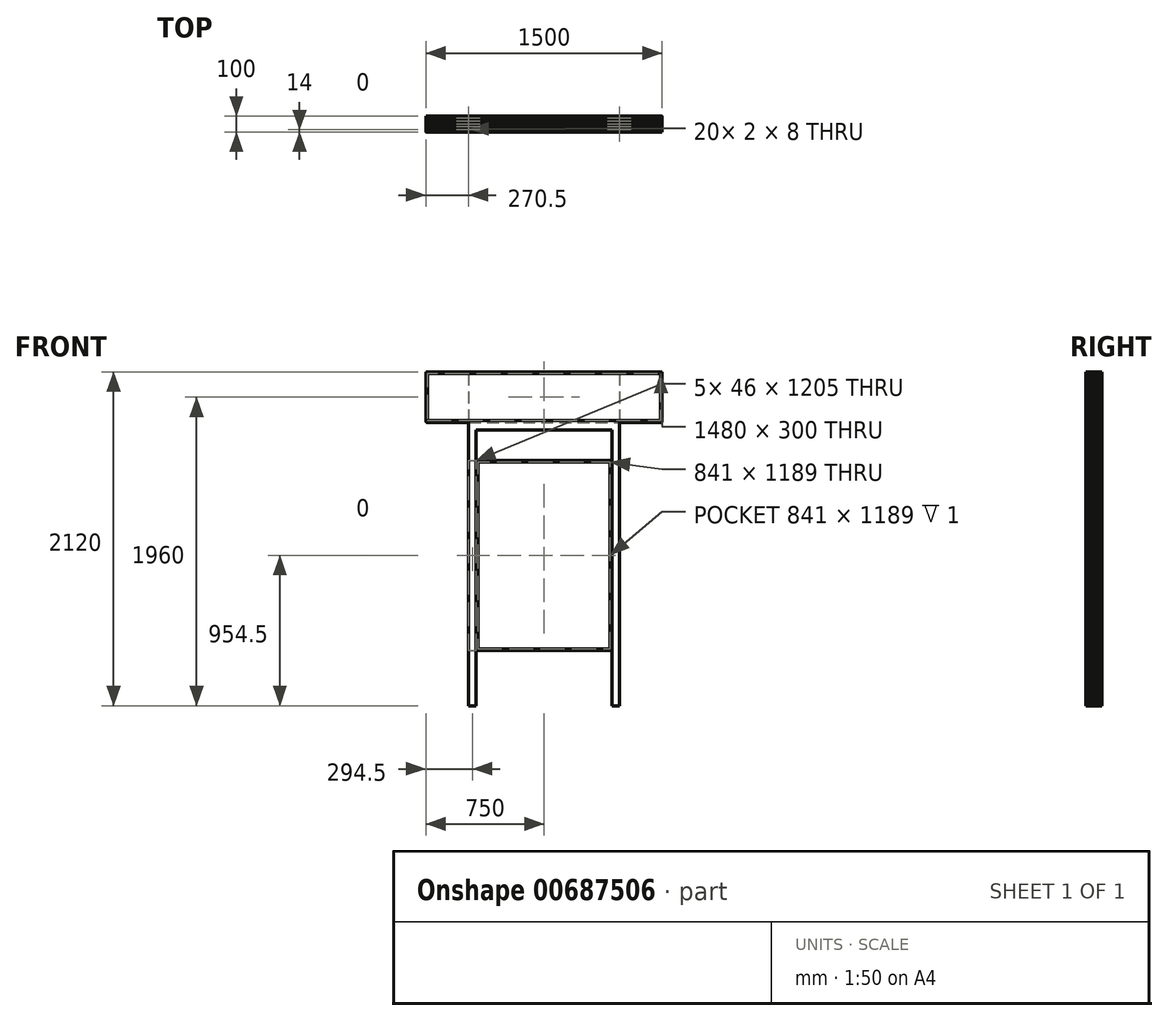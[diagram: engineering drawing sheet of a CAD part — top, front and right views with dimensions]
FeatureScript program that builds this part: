
annotation { "Feature Type Name" : "Feature", "Feature Type Description" : "" }
export const myFeature = defineFeature(function(context is Context, id is Id, definition is map)
    precondition{}
    {
        {
            var Q0;
            Q0=qCreatedBy(makeId("Front.planeOp"),FACE);
            var sketch = newSketch(context, id + "F0", { "sketchPlane" : qUnion([Q0])});
            skLineSegment(sketch, "E0.bottom", {"start": v(-480.5, 0) * mm, "end": v(-430.5, 0) * mm});
            skLineSegment(sketch, "E0.top", {"start": v(-480.5, -1800) * mm, "end": v(-430.5, -1800) * mm});
            skLineSegment(sketch, "E0.left", {"start": v(-480.5, 0) * mm, "end": v(-480.5, -1800) * mm});
            skLineSegment(sketch, "E0.right", {"start": v(-430.5, 0) * mm, "end": v(-430.5, -1800) * mm});
            skLineSegment(sketch, "E1.MirrorCS", {"start": v(480.5, -1800) * mm, "end": v(430.5, -1800) * mm});
            skLineSegment(sketch, "E2.MirrorCS", {"start": v(430.5, 0) * mm, "end": v(430.5, -1800) * mm});
            skLineSegment(sketch, "E3.MirrorCS", {"start": v(480.5, 0) * mm, "end": v(430.5, 0) * mm});
            skLineSegment(sketch, "E4.MirrorCS", {"start": v(480.5, 0) * mm, "end": v(480.5, -1800) * mm});
            skSolve(sketch);
        }
        {
            var Q0;
            Q0=qSketchRegion(id+"F0",true);
            extrude(context, id + "F1", {"entities" : qUnion([Q0]), "depth" : 100 * mm, "offsetDistance" : 25 * mm});
        }
        {
            var Q0;
            Q0=makeQuery(id+"F1.opExtrude","SWEPT_FACE",FACE,{"disambiguationData":[OSD([sQuery(id+"F0.wireOp",EDGE,"E0.bottom")])]});
            var sketch = newSketch(context, id + "F2", { "sketchPlane" : qUnion([Q0])});
            skLineSegment(sketch, "E5.bottom", {"start": v(-750, 0) * mm, "end": v(750, 0) * mm});
            skLineSegment(sketch, "E5.top", {"start": v(-750, -100) * mm, "end": v(750, -100) * mm});
            skLineSegment(sketch, "E5.left", {"start": v(-750, 0) * mm, "end": v(-750, -100) * mm});
            skLineSegment(sketch, "E5.right", {"start": v(750, 0) * mm, "end": v(750, -100) * mm});
            skSolve(sketch);
        }
        {
            var Q0;
            Q0=qSketchRegion(id+"F2",true);
            extrude(context, id + "F3", {"entities" : qUnion([Q0]), "depth" : 320 * mm, "offsetDistance" : 25 * mm});
        }
        {
            var Q0;
            Q0=makeQuery(id+"F3.opExtrude","SWEPT_FACE",FACE,{"disambiguationData":[OSD([sQuery(id+"F2.wireOp",EDGE,"E5.top")])]});
            var sketch = newSketch(context, id + "F4", { "sketchPlane" : qUnion([Q0])});
            skLineSegment(sketch, "E6.0", {"start": v(740, 310) * mm, "end": v(-740, 310) * mm});
            skLineSegment(sketch, "E6.1", {"start": v(740, 10) * mm, "end": v(740, 310) * mm});
            skLineSegment(sketch, "E6.2", {"start": v(-740, 10) * mm, "end": v(740, 10) * mm});
            skLineSegment(sketch, "E6.3", {"start": v(-740, 310) * mm, "end": v(-740, 10) * mm});
            skSolve(sketch);
        }
        {
            var Q0;
            Q0=qSketchRegion(id+"F4",true);
            extrude(context, id + "F5", {"entities" : qUnion([Q0]), "operationType" : NewBodyOperationType.REMOVE, "endBound" : BoundingType.THROUGH_ALL, "oppositeDirection" : true, "depth" : 25 * mm, "offsetDistance" : 25 * mm});
        }
        {
            var Q0;
            Q0=makeQuery(id+"F3.opExtrude","SWEPT_FACE",FACE,{"disambiguationData":[OSD([sQuery(id+"F2.wireOp",EDGE,"E5.right")])]});
            var sketch = newSketch(context, id + "F6", { "sketchPlane" : qUnion([Q0])});
            skLineSegment(sketch, "E7", {"start": v(-90, 320) * mm, "end": v(-90, 318) * mm});
            skLineSegment(sketch, "E8", {"start": v(-90, 318) * mm, "end": v(-82, 318) * mm});
            skLineSegment(sketch, "E9", {"start": v(-82, 318) * mm, "end": v(-82, 320) * mm});
            skLineSegment(sketch, "E10.1.0.0", {"start": v(-64, 318) * mm, "end": v(-64, 320) * mm});
            skLineSegment(sketch, "E10.1.0.1", {"start": v(-72, 318) * mm, "end": v(-64, 318) * mm});
            skLineSegment(sketch, "E10.1.0.2", {"start": v(-72, 320) * mm, "end": v(-72, 318) * mm});
            skLineSegment(sketch, "E10.2.0.0", {"start": v(-46, 318) * mm, "end": v(-46, 320) * mm});
            skLineSegment(sketch, "E10.2.0.1", {"start": v(-54, 318) * mm, "end": v(-46, 318) * mm});
            skLineSegment(sketch, "E10.2.0.2", {"start": v(-54, 320) * mm, "end": v(-54, 318) * mm});
            skLineSegment(sketch, "E10.3.0.0", {"start": v(-28, 318) * mm, "end": v(-28, 320) * mm});
            skLineSegment(sketch, "E10.3.0.1", {"start": v(-36, 318) * mm, "end": v(-28, 318) * mm});
            skLineSegment(sketch, "E10.3.0.2", {"start": v(-36, 320) * mm, "end": v(-36, 318) * mm});
            skLineSegment(sketch, "E10.4.0.0", {"start": v(-10, 318) * mm, "end": v(-10, 320) * mm});
            skLineSegment(sketch, "E10.4.0.1", {"start": v(-18, 318) * mm, "end": v(-10, 318) * mm});
            skLineSegment(sketch, "E10.4.0.2", {"start": v(-18, 320) * mm, "end": v(-18, 318) * mm});
            skLineSegment(sketch, "E10.direction1", {"start": v(-90, 318) * mm, "end": v(-72, 318) * mm, "construction": true});
            skLineSegment(sketch, "E11", {"start": v(-90, 320) * mm, "end": v(-82, 320) * mm});
            skLineSegment(sketch, "E12", {"start": v(-72, 320) * mm, "end": v(-64, 320) * mm});
            skLineSegment(sketch, "E13", {"start": v(-54, 320) * mm, "end": v(-46, 320) * mm});
            skLineSegment(sketch, "E14", {"start": v(-36, 320) * mm, "end": v(-28, 320) * mm});
            skLineSegment(sketch, "E15", {"start": v(-18, 320) * mm, "end": v(-10, 320) * mm});
            skLineSegment(sketch, "E16", {"start": v(0, 160) * mm, "end": v(-100, 160) * mm, "construction": true});
            skLineSegment(sketch, "E17.MirrorCS", {"start": v(-10, 2) * mm, "end": v(-10, 0) * mm});
            skLineSegment(sketch, "E18.MirrorCS", {"start": v(-36, 0) * mm, "end": v(-36, 2) * mm});
            skLineSegment(sketch, "E19.MirrorCS", {"start": v(-90, 0) * mm, "end": v(-90, 2) * mm});
            skLineSegment(sketch, "E20.MirrorCS", {"start": v(-82, 2) * mm, "end": v(-82, 0) * mm});
            skLineSegment(sketch, "E21.MirrorCS", {"start": v(-64, 2) * mm, "end": v(-64, 0) * mm});
            skLineSegment(sketch, "E22.MirrorCS", {"start": v(-72, 0) * mm, "end": v(-72, 2) * mm});
            skLineSegment(sketch, "E23.MirrorCS", {"start": v(-46, 2) * mm, "end": v(-46, 0) * mm});
            skLineSegment(sketch, "E24.MirrorCS", {"start": v(-54, 0) * mm, "end": v(-54, 2) * mm});
            skLineSegment(sketch, "E25.MirrorCS", {"start": v(-28, 2) * mm, "end": v(-28, 0) * mm});
            skLineSegment(sketch, "E26.MirrorCS", {"start": v(-18, 0) * mm, "end": v(-18, 2) * mm});
            skLineSegment(sketch, "E27.MirrorCS", {"start": v(-90, 0) * mm, "end": v(-82, 0) * mm});
            skLineSegment(sketch, "E28.MirrorCS", {"start": v(-90, 2) * mm, "end": v(-82, 2) * mm});
            skLineSegment(sketch, "E29.MirrorCS", {"start": v(-36, 2) * mm, "end": v(-28, 2) * mm});
            skLineSegment(sketch, "E30.MirrorCS", {"start": v(-36, 0) * mm, "end": v(-28, 0) * mm});
            skLineSegment(sketch, "E31.MirrorCS", {"start": v(-18, 0) * mm, "end": v(-10, 0) * mm});
            skLineSegment(sketch, "E32.MirrorCS", {"start": v(-72, 0) * mm, "end": v(-64, 0) * mm});
            skLineSegment(sketch, "E33.MirrorCS", {"start": v(-18, 2) * mm, "end": v(-10, 2) * mm});
            skLineSegment(sketch, "E34.MirrorCS", {"start": v(-90, 2) * mm, "end": v(-72, 2) * mm, "construction": true});
            skLineSegment(sketch, "E35.MirrorCS", {"start": v(-54, 0) * mm, "end": v(-46, 0) * mm});
            skLineSegment(sketch, "E36.MirrorCS", {"start": v(-72, 2) * mm, "end": v(-64, 2) * mm});
            skLineSegment(sketch, "E37.MirrorCS", {"start": v(-54, 2) * mm, "end": v(-46, 2) * mm});
            skSolve(sketch);
        }
        {
            var Q0;
            Q0=qSketchRegion(id+"F6",true);
            extrude(context, id + "F7", {"entities" : qUnion([Q0]), "operationType" : NewBodyOperationType.REMOVE, "endBound" : BoundingType.THROUGH_ALL, "oppositeDirection" : true, "depth" : 25 * mm, "offsetDistance" : 25 * mm});
        }
        {
            var Q0;
            Q0=makeQuery(id+"F3.opExtrude","SWEPT_FACE",FACE,{"disambiguationData":[OSD([sQuery(id+"F2.wireOp",EDGE,"E5.top")])]});
            cPlane(context, id + "F8", {"entities" : qUnion([Q0]), "cplaneType" : CPlaneType.OFFSET, "offset" : 1 * mm, "oppositeDirection" : true, "width" : 150 * mm, "height" : 150 * mm});
        }
        {
            var Q0;
            Q0=qCreatedBy(id+"F8.planeOp",FACE);
            var sketch = newSketch(context, id + "F9", { "sketchPlane" : qUnion([Q0])});
            skLineSegment(sketch, "E38.0", {"start": v(-740, 10) * mm, "end": v(740, 10) * mm});
            skLineSegment(sketch, "E38.1", {"start": v(-740, 310) * mm, "end": v(-740, 10) * mm});
            skLineSegment(sketch, "E38.2", {"start": v(740, 310) * mm, "end": v(-740, 310) * mm});
            skLineSegment(sketch, "E38.3", {"start": v(740, 10) * mm, "end": v(740, 310) * mm});
            skSolve(sketch);
        }
        {
            var Q0;
            Q0=qSketchRegion(id+"F9",true);
            var Q1;
            Q1=makeQuery(id+"F3.opExtrude","SWEPT_FACE",FACE,{"disambiguationData":[OSD([sQuery(id+"F2.wireOp",EDGE,"E5.bottom")])]});
            extrude(context, id + "F10", {"entities" : qUnion([Q0]), "endBound" : BoundingType.UP_TO_SURFACE, "oppositeDirection" : true, "depth" : 25 * mm, "endBoundEntityFace" : qUnion([Q1]), "hasOffset" : true, "offsetDistance" : 1 * mm});
        }
        {
            var Q0;
            {var subQ0=sQuery(id+"F2.wireOp",EDGE,"E5.top");var subQ1=sQuery(id+"F2.wireOp",EDGE,"E5.left");var subQ2=sQuery(id+"F2.wireOp",EDGE,"E5.right");Q0=makeQuery(id+"F7.boolean.opBoolean","SPLIT",FACE,{"disambiguationData":[TD([makeQuery(id+"F3.opExtrude","SWEPT_FACE",FACE,{"disambiguationData":[OSD([subQ0])]})])],"derivedFrom":makeQuery(id+"F3.opExtrude","CAP_FACE",FACE,{"disambiguationData":[OSD([sQuery(id+"F2.wireOp",EDGE,"E5.bottom"),subQ0,subQ1,subQ2])],"isStart":false})});}
            var sketch = newSketch(context, id + "F11", { "sketchPlane" : qUnion([Q0])});
            skLineSegment(sketch, "E39.0", {"start": v(-750, -18) * mm, "end": v(-750, -10) * mm});
            skLineSegment(sketch, "E39.1", {"start": v(-750, -36) * mm, "end": v(-750, -28) * mm});
            skLineSegment(sketch, "E39.2", {"start": v(-750, -54) * mm, "end": v(-750, -46) * mm});
            skLineSegment(sketch, "E39.3", {"start": v(-750, -72) * mm, "end": v(-750, -64) * mm});
            skLineSegment(sketch, "E39.4", {"start": v(-750, -90) * mm, "end": v(-750, -82) * mm});
            skLineSegment(sketch, "E40", {"start": v(-750, -10) * mm, "end": v(-748, -10) * mm});
            skLineSegment(sketch, "E41", {"start": v(-748, -10) * mm, "end": v(-748, -18) * mm});
            skLineSegment(sketch, "E42", {"start": v(-748, -90) * mm, "end": v(-750, -90) * mm});
            skLineSegment(sketch, "E43.0", {"start": v(-750, -18) * mm, "end": v(-748, -18) * mm});
            skLineSegment(sketch, "E43.1", {"start": v(-750, -28) * mm, "end": v(-748, -28) * mm});
            skLineSegment(sketch, "E43.2", {"start": v(-750, -36) * mm, "end": v(-748, -36) * mm});
            skLineSegment(sketch, "E43.3", {"start": v(-750, -46) * mm, "end": v(-748, -46) * mm});
            skLineSegment(sketch, "E43.4", {"start": v(-750, -54) * mm, "end": v(-748, -54) * mm});
            skLineSegment(sketch, "E43.5", {"start": v(-750, -64) * mm, "end": v(-748, -64) * mm});
            skLineSegment(sketch, "E43.6", {"start": v(-750, -72) * mm, "end": v(-748, -72) * mm});
            skLineSegment(sketch, "E43.7", {"start": v(-750, -82) * mm, "end": v(-748, -82) * mm});
            skLineSegment(sketch, "E44.trimOffspring", {"start": v(-748, -82) * mm, "end": v(-748, -90) * mm});
            skPoint(sketch, "E45.orphan", {"position": v(750, -82) * mm});
            skPoint(sketch, "E46.orphan", {"position": v(750, -72) * mm});
            skPoint(sketch, "E47.orphan", {"position": v(750, -64) * mm});
            skLineSegment(sketch, "E48.trimOffspring", {"start": v(-748, -64) * mm, "end": v(-748, -72) * mm});
            skPoint(sketch, "E49.orphan", {"position": v(750, -54) * mm});
            skPoint(sketch, "E50.orphan", {"position": v(750, -46) * mm});
            skLineSegment(sketch, "E51.trimOffspring", {"start": v(-748, -46) * mm, "end": v(-748, -54) * mm});
            skPoint(sketch, "E52.orphan", {"position": v(750, -36) * mm});
            skPoint(sketch, "E53.orphan", {"position": v(750, -28) * mm});
            skLineSegment(sketch, "E54.trimOffspring", {"start": v(-748, -28) * mm, "end": v(-748, -36) * mm});
            skPoint(sketch, "E55.orphan", {"position": v(750, -18) * mm});
            skLineSegment(sketch, "E56.MirrorCS", {"start": v(748, -46) * mm, "end": v(748, -54) * mm});
            skLineSegment(sketch, "E57.MirrorCS", {"start": v(748, -28) * mm, "end": v(748, -36) * mm});
            skLineSegment(sketch, "E58.MirrorCS", {"start": v(750, -64) * mm, "end": v(748, -64) * mm});
            skLineSegment(sketch, "E59.MirrorCS", {"start": v(750, -46) * mm, "end": v(748, -46) * mm});
            skLineSegment(sketch, "E60.MirrorCS", {"start": v(750, -54) * mm, "end": v(748, -54) * mm});
            skLineSegment(sketch, "E61.MirrorCS", {"start": v(750, -28) * mm, "end": v(748, -28) * mm});
            skLineSegment(sketch, "E62.MirrorCS", {"start": v(750, -36) * mm, "end": v(748, -36) * mm});
            skLineSegment(sketch, "E63.MirrorCS", {"start": v(750, -54) * mm, "end": v(750, -46) * mm});
            skLineSegment(sketch, "E64.MirrorCS", {"start": v(750, -36) * mm, "end": v(750, -28) * mm});
            skLineSegment(sketch, "E65.MirrorCS", {"start": v(750, -10) * mm, "end": v(748, -10) * mm});
            skLineSegment(sketch, "E66.MirrorCS", {"start": v(748, -64) * mm, "end": v(748, -72) * mm});
            skLineSegment(sketch, "E67.MirrorCS", {"start": v(750, -18) * mm, "end": v(748, -18) * mm});
            skLineSegment(sketch, "E68.MirrorCS", {"start": v(750, -72) * mm, "end": v(748, -72) * mm});
            skLineSegment(sketch, "E69.MirrorCS", {"start": v(748, -10) * mm, "end": v(748, -18) * mm});
            skLineSegment(sketch, "E70.MirrorCS", {"start": v(750, -72) * mm, "end": v(750, -64) * mm});
            skLineSegment(sketch, "E71.MirrorCS", {"start": v(748, -90) * mm, "end": v(750, -90) * mm});
            skLineSegment(sketch, "E72.MirrorCS", {"start": v(750, -82) * mm, "end": v(748, -82) * mm});
            skLineSegment(sketch, "E73.MirrorCS", {"start": v(750, -18) * mm, "end": v(750, -10) * mm});
            skLineSegment(sketch, "E74.MirrorCS", {"start": v(750, -90) * mm, "end": v(750, -82) * mm});
            skLineSegment(sketch, "E75.MirrorCS", {"start": v(748, -82) * mm, "end": v(748, -90) * mm});
            skSolve(sketch);
        }
        {
            var Q0;
            Q0 = qSketchRegion(id + "F11", true);
            extrude(context, id + "F12", {"entities" : qUnion([Q0]), "operationType" : NewBodyOperationType.REMOVE, "endBound" : BoundingType.THROUGH_ALL, "oppositeDirection" : true, "depth" : 25 * mm, "offsetDistance" : 25 * mm});
        }
        {
            var Q0;
            Q0=makeQuery(id+"F1.opExtrude","CAP_FACE",FACE,{"disambiguationData":[OSD([sQuery(id+"F0.wireOp",EDGE,"E1.MirrorCS"),sQuery(id+"F0.wireOp",EDGE,"E2.MirrorCS"),sQuery(id+"F0.wireOp",EDGE,"E3.MirrorCS"),sQuery(id+"F0.wireOp",EDGE,"E4.MirrorCS")])],"isStart":true});
            var sketch = newSketch(context, id + "F13", { "sketchPlane" : qUnion([Q0])});
            skLineSegment(sketch, "E76.bottom", {"start": v(-430.5, 0) * mm, "end": v(430.5, 0) * mm});
            skLineSegment(sketch, "E76.top", {"start": v(-430.5, -50) * mm, "end": v(430.5, -50) * mm});
            skLineSegment(sketch, "E76.left", {"start": v(-430.5, 0) * mm, "end": v(-430.5, -50) * mm});
            skLineSegment(sketch, "E76.right", {"start": v(430.5, 0) * mm, "end": v(430.5, -50) * mm});
            skSolve(sketch);
        }
        {
            var Q0;
            Q0 = qSketchRegion(id + "F13", true);
            var Q1;
            Q1=makeQuery(id+"F1.opExtrude","CAP_FACE",FACE,{"disambiguationData":[OSD([sQuery(id+"F0.wireOp",EDGE,"E0.bottom"),sQuery(id+"F0.wireOp",EDGE,"E0.top"),sQuery(id+"F0.wireOp",EDGE,"E0.left"),sQuery(id+"F0.wireOp",EDGE,"E0.right")])],"isStart":false});
            extrude(context, id + "F14", {"entities" : qUnion([Q0]), "operationType" : NewBodyOperationType.ADD, "endBound" : BoundingType.UP_TO_SURFACE, "oppositeDirection" : true, "depth" : 25 * mm, "endBoundEntityFace" : qUnion([Q1]), "offsetDistance" : 25 * mm});
        }
        {
            var Q0;
            Q0=makeQuery(id+"F14.boolean.opBoolean","MERGE",FACE,{"derivedFrom":[makeQuery(id+"F1.opExtrude","CAP_FACE",FACE,{"disambiguationData":[OSD([sQuery(id+"F0.wireOp",EDGE,"E0.bottom"),sQuery(id+"F0.wireOp",EDGE,"E0.top"),sQuery(id+"F0.wireOp",EDGE,"E0.left"),sQuery(id+"F0.wireOp",EDGE,"E0.right")])],"isStart":false}),makeQuery(id+"F1.opExtrude","CAP_FACE",FACE,{"disambiguationData":[OSD([sQuery(id+"F0.wireOp",EDGE,"E1.MirrorCS"),sQuery(id+"F0.wireOp",EDGE,"E2.MirrorCS"),sQuery(id+"F0.wireOp",EDGE,"E3.MirrorCS"),sQuery(id+"F0.wireOp",EDGE,"E4.MirrorCS")])],"isStart":false}),makeQuery(id+"F14.opExtrude","CAP_FACE",FACE,{"disambiguationData":[OSD([sQuery(id+"F13.wireOp",EDGE,"E76.bottom"),sQuery(id+"F13.wireOp",EDGE,"E76.top"),sQuery(id+"F13.wireOp",EDGE,"E76.left"),sQuery(id+"F13.wireOp",EDGE,"E76.right")])],"isStart":false})]});
            var sketch = newSketch(context, id + "F15", { "sketchPlane" : qUnion([Q0])});
            skLineSegment(sketch, "E77.bottom", {"start": v(-430.5, -241) * mm, "end": v(430.5, -241) * mm});
            skLineSegment(sketch, "E77.top", {"start": v(-430.5, -1450) * mm, "end": v(430.5, -1450) * mm});
            skLineSegment(sketch, "E77.left", {"start": v(-430.5, -241) * mm, "end": v(-430.5, -1450) * mm});
            skLineSegment(sketch, "E77.right", {"start": v(430.5, -241) * mm, "end": v(430.5, -1450) * mm});
            skLineSegment(sketch, "E78.0", {"start": v(-420.5, -251) * mm, "end": v(-420.5, -1440) * mm});
            skLineSegment(sketch, "E78.1", {"start": v(-420.5, -251) * mm, "end": v(420.5, -251) * mm});
            skLineSegment(sketch, "E78.2", {"start": v(420.5, -251) * mm, "end": v(420.5, -1440) * mm});
            skLineSegment(sketch, "E78.3", {"start": v(-420.5, -1440) * mm, "end": v(420.5, -1440) * mm});
            skSolve(sketch);
        }
        {
            var Q0;
            Q0 = qSketchRegion(id + "F15", true);
            extrude(context, id + "F16", {"entities" : qUnion([Q0]), "oppositeDirection" : true, "depth" : 100 * mm, "offsetDistance" : 25 * mm});
        }
        {
            var Q0;
            Q0=makeQuery(id+"F10.opExtrude","CAP_FACE",FACE,{"disambiguationData":[OSD([sQuery(id+"F9.wireOp",EDGE,"E38.0"),sQuery(id+"F9.wireOp",EDGE,"E38.1"),sQuery(id+"F9.wireOp",EDGE,"E38.2"),sQuery(id+"F9.wireOp",EDGE,"E38.3")])],"isStart":true});
            var sketch = newSketch(context, id + "F17", { "sketchPlane" : qUnion([Q0])});
            skLineSegment(sketch, "E79.0", {"start": v(-420.5, -251) * mm, "end": v(420.5, -251) * mm});
            skLineSegment(sketch, "E79.1", {"start": v(-420.5, -251) * mm, "end": v(-420.5, -1440) * mm});
            skLineSegment(sketch, "E79.2", {"start": v(-420.5, -1440) * mm, "end": v(420.5, -1440) * mm});
            skLineSegment(sketch, "E79.3", {"start": v(420.5, -251) * mm, "end": v(420.5, -1440) * mm});
            skSolve(sketch);
        }
        {
            var Q0;
            Q0 = qSketchRegion(id + "F17", true);
            var Q1;
            Q1=makeQuery(id+"F16.opExtrude","CAP_FACE",FACE,{"disambiguationData":[OSD([sQuery(id+"F15.wireOp",EDGE,"E77.bottom"),sQuery(id+"F15.wireOp",EDGE,"E77.top"),sQuery(id+"F15.wireOp",EDGE,"E77.left"),sQuery(id+"F15.wireOp",EDGE,"E77.right"),sQuery(id+"F15.wireOp",EDGE,"E78.0"),sQuery(id+"F15.wireOp",EDGE,"E78.1"),sQuery(id+"F15.wireOp",EDGE,"E78.2"),sQuery(id+"F15.wireOp",EDGE,"E78.3")])],"isStart":false});
            extrude(context, id + "F18", {"entities" : qUnion([Q0]), "operationType" : NewBodyOperationType.ADD, "endBound" : BoundingType.UP_TO_SURFACE, "oppositeDirection" : true, "depth" : 25 * mm, "endBoundEntityFace" : qUnion([Q1]), "hasOffset" : true, "offsetDistance" : 1 * mm});
        }
        {
            var Q0;
            Q0=makeQuery(id+"F16.opExtrude","SWEPT_FACE",FACE,{"disambiguationData":[OSD([sQuery(id+"F15.wireOp",EDGE,"E77.right")])]});
            var sketch = newSketch(context, id + "F19", { "sketchPlane" : qUnion([Q0])});
            skLineSegment(sketch, "E80.bottom", {"start": v(-90, -241) * mm, "end": v(-82, -241) * mm});
            skLineSegment(sketch, "E80.top", {"start": v(-90, -243) * mm, "end": v(-82, -243) * mm});
            skLineSegment(sketch, "E80.left", {"start": v(-90, -241) * mm, "end": v(-90, -243) * mm});
            skLineSegment(sketch, "E80.right", {"start": v(-82, -241) * mm, "end": v(-82, -243) * mm});
            skLineSegment(sketch, "E81.1.0.0", {"start": v(-72, -241) * mm, "end": v(-72, -243) * mm});
            skLineSegment(sketch, "E81.1.0.1", {"start": v(-64, -241) * mm, "end": v(-64, -243) * mm});
            skLineSegment(sketch, "E81.1.0.2", {"start": v(-72, -243) * mm, "end": v(-64, -243) * mm});
            skLineSegment(sketch, "E81.1.0.3", {"start": v(-72, -241) * mm, "end": v(-64, -241) * mm});
            skLineSegment(sketch, "E81.2.0.0", {"start": v(-54, -241) * mm, "end": v(-54, -243) * mm});
            skLineSegment(sketch, "E81.2.0.1", {"start": v(-46, -241) * mm, "end": v(-46, -243) * mm});
            skLineSegment(sketch, "E81.2.0.2", {"start": v(-54, -243) * mm, "end": v(-46, -243) * mm});
            skLineSegment(sketch, "E81.2.0.3", {"start": v(-54, -241) * mm, "end": v(-46, -241) * mm});
            skLineSegment(sketch, "E81.3.0.0", {"start": v(-36, -241) * mm, "end": v(-36, -243) * mm});
            skLineSegment(sketch, "E81.3.0.1", {"start": v(-28, -241) * mm, "end": v(-28, -243) * mm});
            skLineSegment(sketch, "E81.3.0.2", {"start": v(-36, -243) * mm, "end": v(-28, -243) * mm});
            skLineSegment(sketch, "E81.3.0.3", {"start": v(-36, -241) * mm, "end": v(-28, -241) * mm});
            skLineSegment(sketch, "E81.4.0.0", {"start": v(-18, -241) * mm, "end": v(-18, -243) * mm});
            skLineSegment(sketch, "E81.4.0.1", {"start": v(-10, -241) * mm, "end": v(-10, -243) * mm});
            skLineSegment(sketch, "E81.4.0.2", {"start": v(-18, -243) * mm, "end": v(-10, -243) * mm});
            skLineSegment(sketch, "E81.4.0.3", {"start": v(-18, -241) * mm, "end": v(-10, -241) * mm});
            skLineSegment(sketch, "E81.direction1", {"start": v(-90, -243) * mm, "end": v(-72, -243) * mm, "construction": true});
            skLineSegment(sketch, "E82", {"start": v(-100, -845.5) * mm, "end": v(0, -845.5) * mm, "construction": true});
            skLineSegment(sketch, "E83.MirrorCS", {"start": v(-90, -1450) * mm, "end": v(-90, -1448) * mm});
            skLineSegment(sketch, "E84.MirrorCS", {"start": v(-64, -1450) * mm, "end": v(-64, -1448) * mm});
            skLineSegment(sketch, "E85.MirrorCS", {"start": v(-90, -1448) * mm, "end": v(-82, -1448) * mm});
            skLineSegment(sketch, "E86.MirrorCS", {"start": v(-54, -1450) * mm, "end": v(-54, -1448) * mm});
            skLineSegment(sketch, "E87.MirrorCS", {"start": v(-18, -1450) * mm, "end": v(-18, -1448) * mm});
            skLineSegment(sketch, "E88.MirrorCS", {"start": v(-72, -1450) * mm, "end": v(-72, -1448) * mm});
            skLineSegment(sketch, "E89.MirrorCS", {"start": v(-10, -1450) * mm, "end": v(-10, -1448) * mm});
            skLineSegment(sketch, "E90.MirrorCS", {"start": v(-36, -1450) * mm, "end": v(-28, -1450) * mm});
            skLineSegment(sketch, "E91.MirrorCS", {"start": v(-36, -1448) * mm, "end": v(-28, -1448) * mm});
            skLineSegment(sketch, "E92.MirrorCS", {"start": v(-72, -1448) * mm, "end": v(-64, -1448) * mm});
            skLineSegment(sketch, "E93.MirrorCS", {"start": v(-18, -1448) * mm, "end": v(-10, -1448) * mm});
            skLineSegment(sketch, "E94.MirrorCS", {"start": v(-46, -1450) * mm, "end": v(-46, -1448) * mm});
            skLineSegment(sketch, "E95.MirrorCS", {"start": v(-72, -1450) * mm, "end": v(-64, -1450) * mm});
            skLineSegment(sketch, "E96.MirrorCS", {"start": v(-90, -1448) * mm, "end": v(-72, -1448) * mm, "construction": true});
            skLineSegment(sketch, "E97.MirrorCS", {"start": v(-90, -1450) * mm, "end": v(-82, -1450) * mm});
            skLineSegment(sketch, "E98.MirrorCS", {"start": v(-54, -1448) * mm, "end": v(-46, -1448) * mm});
            skLineSegment(sketch, "E99.MirrorCS", {"start": v(-36, -1450) * mm, "end": v(-36, -1448) * mm});
            skLineSegment(sketch, "E100.MirrorCS", {"start": v(-82, -1450) * mm, "end": v(-82, -1448) * mm});
            skLineSegment(sketch, "E101.MirrorCS", {"start": v(-28, -1450) * mm, "end": v(-28, -1448) * mm});
            skLineSegment(sketch, "E102.MirrorCS", {"start": v(-54, -1450) * mm, "end": v(-46, -1450) * mm});
            skLineSegment(sketch, "E103.MirrorCS", {"start": v(-18, -1450) * mm, "end": v(-10, -1450) * mm});
            skSolve(sketch);
        }
        {
            var Q0;
            Q0 = qSketchRegion(id + "F19", true);
            extrude(context, id + "F20", {"entities" : qUnion([Q0]), "operationType" : NewBodyOperationType.REMOVE, "endBound" : BoundingType.THROUGH_ALL, "oppositeDirection" : true, "depth" : 25 * mm, "offsetDistance" : 25 * mm});
        }
        {
            var Q0;
            {var subQ0=sQuery(id+"F2.wireOp",EDGE,"E5.right");var subQ1=sQuery(id+"F2.wireOp",EDGE,"E5.top");Q0=makeQuery(id+"F7.boolean.opBoolean","SPLIT",EDGE,{"disambiguationData":[TD([makeQuery(id+"F3.opExtrude","SWEPT_FACE",FACE,{"disambiguationData":[OSD([subQ1])]})])],"derivedFrom":makeQuery(id+"F3.opExtrude","CAP_EDGE",EDGE,{"disambiguationData":[OSD([subQ0])],"isStart":true})});}
            var Q1;
            Q1=makeQuery(id+"F12.boolean.opBoolean","INTERSECT",EDGE,{"derivedFrom":[makeQuery(id+"F7.boolean.opBoolean","COPY",FACE,{"derivedFrom":makeQuery(id+"F7.opExtrude","SWEPT_FACE",FACE,{"disambiguationData":[OSD([sQuery(id+"F6.wireOp",EDGE,"E28.MirrorCS")])]})}),makeQuery(id+"F12.opExtrude","SWEPT_FACE",FACE,{"disambiguationData":[OSD([sQuery(id+"F11.wireOp",EDGE,"E75.MirrorCS")])]})]});
            var Q2;
            {var subQ0=sQuery(id+"F2.wireOp",EDGE,"E5.right");Q2=makeQuery(id+"F7.boolean.opBoolean","SPLIT",EDGE,{"disambiguationData":[TD([makeQuery(id+"F7.opExtrude","SWEPT_FACE",FACE,{"disambiguationData":[OSD([sQuery(id+"F6.wireOp",EDGE,"E20.MirrorCS")])]})])],"derivedFrom":makeQuery(id+"F3.opExtrude","CAP_EDGE",EDGE,{"disambiguationData":[OSD([subQ0])],"isStart":true})});}
            var Q3;
            Q3=makeQuery(id+"F12.boolean.opBoolean","INTERSECT",EDGE,{"derivedFrom":[makeQuery(id+"F7.boolean.opBoolean","COPY",FACE,{"derivedFrom":makeQuery(id+"F7.opExtrude","SWEPT_FACE",FACE,{"disambiguationData":[OSD([sQuery(id+"F6.wireOp",EDGE,"E36.MirrorCS")])]})}),makeQuery(id+"F12.opExtrude","SWEPT_FACE",FACE,{"disambiguationData":[OSD([sQuery(id+"F11.wireOp",EDGE,"E66.MirrorCS")])]})]});
            var Q4;
            {var subQ0=sQuery(id+"F2.wireOp",EDGE,"E5.right");Q4=makeQuery(id+"F7.boolean.opBoolean","SPLIT",EDGE,{"disambiguationData":[TD([makeQuery(id+"F7.opExtrude","SWEPT_FACE",FACE,{"disambiguationData":[OSD([sQuery(id+"F6.wireOp",EDGE,"E21.MirrorCS")])]})])],"derivedFrom":makeQuery(id+"F3.opExtrude","CAP_EDGE",EDGE,{"disambiguationData":[OSD([subQ0])],"isStart":true})});}
            var Q5;
            Q5=makeQuery(id+"F12.boolean.opBoolean","INTERSECT",EDGE,{"derivedFrom":[makeQuery(id+"F7.boolean.opBoolean","COPY",FACE,{"derivedFrom":makeQuery(id+"F7.opExtrude","SWEPT_FACE",FACE,{"disambiguationData":[OSD([sQuery(id+"F6.wireOp",EDGE,"E37.MirrorCS")])]})}),makeQuery(id+"F12.opExtrude","SWEPT_FACE",FACE,{"disambiguationData":[OSD([sQuery(id+"F11.wireOp",EDGE,"E56.MirrorCS")])]})]});
            var Q6;
            {var subQ0=sQuery(id+"F2.wireOp",EDGE,"E5.right");Q6=makeQuery(id+"F7.boolean.opBoolean","SPLIT",EDGE,{"disambiguationData":[TD([makeQuery(id+"F7.opExtrude","SWEPT_FACE",FACE,{"disambiguationData":[OSD([sQuery(id+"F6.wireOp",EDGE,"E18.MirrorCS")])]})])],"derivedFrom":makeQuery(id+"F3.opExtrude","CAP_EDGE",EDGE,{"disambiguationData":[OSD([subQ0])],"isStart":true})});}
            var Q7;
            Q7=makeQuery(id+"F12.boolean.opBoolean","INTERSECT",EDGE,{"derivedFrom":[makeQuery(id+"F7.boolean.opBoolean","COPY",FACE,{"derivedFrom":makeQuery(id+"F7.opExtrude","SWEPT_FACE",FACE,{"disambiguationData":[OSD([sQuery(id+"F6.wireOp",EDGE,"E29.MirrorCS")])]})}),makeQuery(id+"F12.opExtrude","SWEPT_FACE",FACE,{"disambiguationData":[OSD([sQuery(id+"F11.wireOp",EDGE,"E57.MirrorCS")])]})]});
            var Q8;
            {var subQ0=sQuery(id+"F2.wireOp",EDGE,"E5.right");Q8=makeQuery(id+"F7.boolean.opBoolean","SPLIT",EDGE,{"disambiguationData":[TD([makeQuery(id+"F7.opExtrude","SWEPT_FACE",FACE,{"disambiguationData":[OSD([sQuery(id+"F6.wireOp",EDGE,"E25.MirrorCS")])]})])],"derivedFrom":makeQuery(id+"F3.opExtrude","CAP_EDGE",EDGE,{"disambiguationData":[OSD([subQ0])],"isStart":true})});}
            var Q9;
            Q9=makeQuery(id+"F12.boolean.opBoolean","INTERSECT",EDGE,{"derivedFrom":[makeQuery(id+"F7.boolean.opBoolean","COPY",FACE,{"derivedFrom":makeQuery(id+"F7.opExtrude","SWEPT_FACE",FACE,{"disambiguationData":[OSD([sQuery(id+"F6.wireOp",EDGE,"E33.MirrorCS")])]})}),makeQuery(id+"F12.opExtrude","SWEPT_FACE",FACE,{"disambiguationData":[OSD([sQuery(id+"F11.wireOp",EDGE,"E69.MirrorCS")])]})]});
            var Q10;
            {var subQ0=sQuery(id+"F2.wireOp",EDGE,"E5.bottom");var subQ1=sQuery(id+"F2.wireOp",EDGE,"E5.right");Q10=makeQuery(id+"F7.boolean.opBoolean","SPLIT",EDGE,{"disambiguationData":[TD([makeQuery(id+"F3.opExtrude","SWEPT_FACE",FACE,{"disambiguationData":[OSD([subQ0])]})])],"derivedFrom":makeQuery(id+"F3.opExtrude","CAP_EDGE",EDGE,{"disambiguationData":[OSD([subQ1])],"isStart":true})});}
            var Q11;
            {var subQ0=sQuery(id+"F2.wireOp",EDGE,"E5.right");var subQ1=sQuery(id+"F2.wireOp",EDGE,"E5.top");Q11=makeQuery(id+"F7.boolean.opBoolean","SPLIT",EDGE,{"disambiguationData":[TD([makeQuery(id+"F3.opExtrude","SWEPT_FACE",FACE,{"disambiguationData":[OSD([subQ1])]})])],"derivedFrom":makeQuery(id+"F3.opExtrude","CAP_EDGE",EDGE,{"disambiguationData":[OSD([subQ0])],"isStart":false})});}
            var Q12;
            Q12=makeQuery(id+"F12.boolean.opBoolean","INTERSECT",EDGE,{"derivedFrom":[makeQuery(id+"F7.boolean.opBoolean","COPY",FACE,{"derivedFrom":makeQuery(id+"F7.opExtrude","SWEPT_FACE",FACE,{"disambiguationData":[OSD([sQuery(id+"F6.wireOp",EDGE,"E8")])]})}),makeQuery(id+"F12.opExtrude","SWEPT_FACE",FACE,{"disambiguationData":[OSD([sQuery(id+"F11.wireOp",EDGE,"E75.MirrorCS")])]})]});
            var Q13;
            {var subQ0=sQuery(id+"F2.wireOp",EDGE,"E5.right");Q13=makeQuery(id+"F7.boolean.opBoolean","SPLIT",EDGE,{"disambiguationData":[TD([makeQuery(id+"F7.opExtrude","SWEPT_FACE",FACE,{"disambiguationData":[OSD([sQuery(id+"F6.wireOp",EDGE,"E9")])]})])],"derivedFrom":makeQuery(id+"F3.opExtrude","CAP_EDGE",EDGE,{"disambiguationData":[OSD([subQ0])],"isStart":false})});}
            var Q14;
            Q14=makeQuery(id+"F12.boolean.opBoolean","INTERSECT",EDGE,{"derivedFrom":[makeQuery(id+"F7.boolean.opBoolean","COPY",FACE,{"derivedFrom":makeQuery(id+"F7.opExtrude","SWEPT_FACE",FACE,{"disambiguationData":[OSD([sQuery(id+"F6.wireOp",EDGE,"E10.1.0.1")])]})}),makeQuery(id+"F12.opExtrude","SWEPT_FACE",FACE,{"disambiguationData":[OSD([sQuery(id+"F11.wireOp",EDGE,"E66.MirrorCS")])]})]});
            var Q15;
            {var subQ0=sQuery(id+"F2.wireOp",EDGE,"E5.right");Q15=makeQuery(id+"F7.boolean.opBoolean","SPLIT",EDGE,{"disambiguationData":[TD([makeQuery(id+"F7.opExtrude","SWEPT_FACE",FACE,{"disambiguationData":[OSD([sQuery(id+"F6.wireOp",EDGE,"E10.1.0.0")])]})])],"derivedFrom":makeQuery(id+"F3.opExtrude","CAP_EDGE",EDGE,{"disambiguationData":[OSD([subQ0])],"isStart":false})});}
            var Q16;
            Q16=makeQuery(id+"F12.boolean.opBoolean","INTERSECT",EDGE,{"derivedFrom":[makeQuery(id+"F7.boolean.opBoolean","COPY",FACE,{"derivedFrom":makeQuery(id+"F7.opExtrude","SWEPT_FACE",FACE,{"disambiguationData":[OSD([sQuery(id+"F6.wireOp",EDGE,"E10.2.0.1")])]})}),makeQuery(id+"F12.opExtrude","SWEPT_FACE",FACE,{"disambiguationData":[OSD([sQuery(id+"F11.wireOp",EDGE,"E56.MirrorCS")])]})]});
            var Q17;
            {var subQ0=sQuery(id+"F2.wireOp",EDGE,"E5.right");Q17=makeQuery(id+"F7.boolean.opBoolean","SPLIT",EDGE,{"disambiguationData":[TD([makeQuery(id+"F7.opExtrude","SWEPT_FACE",FACE,{"disambiguationData":[OSD([sQuery(id+"F6.wireOp",EDGE,"E10.2.0.0")])]})])],"derivedFrom":makeQuery(id+"F3.opExtrude","CAP_EDGE",EDGE,{"disambiguationData":[OSD([subQ0])],"isStart":false})});}
            var Q18;
            Q18=makeQuery(id+"F12.boolean.opBoolean","INTERSECT",EDGE,{"derivedFrom":[makeQuery(id+"F7.boolean.opBoolean","COPY",FACE,{"derivedFrom":makeQuery(id+"F7.opExtrude","SWEPT_FACE",FACE,{"disambiguationData":[OSD([sQuery(id+"F6.wireOp",EDGE,"E10.3.0.1")])]})}),makeQuery(id+"F12.opExtrude","SWEPT_FACE",FACE,{"disambiguationData":[OSD([sQuery(id+"F11.wireOp",EDGE,"E57.MirrorCS")])]})]});
            var Q19;
            {var subQ0=sQuery(id+"F2.wireOp",EDGE,"E5.right");Q19=makeQuery(id+"F7.boolean.opBoolean","SPLIT",EDGE,{"disambiguationData":[TD([makeQuery(id+"F7.opExtrude","SWEPT_FACE",FACE,{"disambiguationData":[OSD([sQuery(id+"F6.wireOp",EDGE,"E10.3.0.0")])]})])],"derivedFrom":makeQuery(id+"F3.opExtrude","CAP_EDGE",EDGE,{"disambiguationData":[OSD([subQ0])],"isStart":false})});}
            var Q20;
            Q20=makeQuery(id+"F12.boolean.opBoolean","INTERSECT",EDGE,{"derivedFrom":[makeQuery(id+"F7.boolean.opBoolean","COPY",FACE,{"derivedFrom":makeQuery(id+"F7.opExtrude","SWEPT_FACE",FACE,{"disambiguationData":[OSD([sQuery(id+"F6.wireOp",EDGE,"E10.4.0.1")])]})}),makeQuery(id+"F12.opExtrude","SWEPT_FACE",FACE,{"disambiguationData":[OSD([sQuery(id+"F11.wireOp",EDGE,"E69.MirrorCS")])]})]});
            var Q21;
            {var subQ0=sQuery(id+"F2.wireOp",EDGE,"E5.bottom");var subQ1=sQuery(id+"F2.wireOp",EDGE,"E5.right");Q21=makeQuery(id+"F7.boolean.opBoolean","SPLIT",EDGE,{"disambiguationData":[TD([makeQuery(id+"F3.opExtrude","SWEPT_FACE",FACE,{"disambiguationData":[OSD([subQ0])]})])],"derivedFrom":makeQuery(id+"F3.opExtrude","CAP_EDGE",EDGE,{"disambiguationData":[OSD([subQ1])],"isStart":false})});}
            var Q22;
            {var subQ0=sQuery(id+"F2.wireOp",EDGE,"E5.bottom");var subQ1=sQuery(id+"F2.wireOp",EDGE,"E5.left");Q22=makeQuery(id+"F7.boolean.opBoolean","SPLIT",EDGE,{"disambiguationData":[TD([makeQuery(id+"F3.opExtrude","SWEPT_FACE",FACE,{"disambiguationData":[OSD([subQ0])]})])],"derivedFrom":makeQuery(id+"F3.opExtrude","CAP_EDGE",EDGE,{"disambiguationData":[OSD([subQ1])],"isStart":false})});}
            var Q23;
            Q23=makeQuery(id+"F12.boolean.opBoolean","INTERSECT",EDGE,{"derivedFrom":[makeQuery(id+"F7.boolean.opBoolean","COPY",FACE,{"derivedFrom":makeQuery(id+"F7.opExtrude","SWEPT_FACE",FACE,{"disambiguationData":[OSD([sQuery(id+"F6.wireOp",EDGE,"E10.4.0.1")])]})}),makeQuery(id+"F12.opExtrude","SWEPT_FACE",FACE,{"disambiguationData":[OSD([sQuery(id+"F11.wireOp",EDGE,"E41")])]})]});
            var Q24;
            {var subQ0=sQuery(id+"F2.wireOp",EDGE,"E5.left");Q24=makeQuery(id+"F7.boolean.opBoolean","SPLIT",EDGE,{"disambiguationData":[TD([makeQuery(id+"F7.opExtrude","SWEPT_FACE",FACE,{"disambiguationData":[OSD([sQuery(id+"F6.wireOp",EDGE,"E10.3.0.0")])]})])],"derivedFrom":makeQuery(id+"F3.opExtrude","CAP_EDGE",EDGE,{"disambiguationData":[OSD([subQ0])],"isStart":false})});}
            var Q25;
            Q25=makeQuery(id+"F12.boolean.opBoolean","INTERSECT",EDGE,{"derivedFrom":[makeQuery(id+"F7.boolean.opBoolean","COPY",FACE,{"derivedFrom":makeQuery(id+"F7.opExtrude","SWEPT_FACE",FACE,{"disambiguationData":[OSD([sQuery(id+"F6.wireOp",EDGE,"E10.3.0.1")])]})}),makeQuery(id+"F12.opExtrude","SWEPT_FACE",FACE,{"disambiguationData":[OSD([sQuery(id+"F11.wireOp",EDGE,"E54.trimOffspring")])]})]});
            var Q26;
            {var subQ0=sQuery(id+"F2.wireOp",EDGE,"E5.left");Q26=makeQuery(id+"F7.boolean.opBoolean","SPLIT",EDGE,{"disambiguationData":[TD([makeQuery(id+"F7.opExtrude","SWEPT_FACE",FACE,{"disambiguationData":[OSD([sQuery(id+"F6.wireOp",EDGE,"E10.2.0.0")])]})])],"derivedFrom":makeQuery(id+"F3.opExtrude","CAP_EDGE",EDGE,{"disambiguationData":[OSD([subQ0])],"isStart":false})});}
            var Q27;
            Q27=makeQuery(id+"F12.boolean.opBoolean","INTERSECT",EDGE,{"derivedFrom":[makeQuery(id+"F7.boolean.opBoolean","COPY",FACE,{"derivedFrom":makeQuery(id+"F7.opExtrude","SWEPT_FACE",FACE,{"disambiguationData":[OSD([sQuery(id+"F6.wireOp",EDGE,"E10.2.0.1")])]})}),makeQuery(id+"F12.opExtrude","SWEPT_FACE",FACE,{"disambiguationData":[OSD([sQuery(id+"F11.wireOp",EDGE,"E51.trimOffspring")])]})]});
            var Q28;
            {var subQ0=sQuery(id+"F2.wireOp",EDGE,"E5.left");Q28=makeQuery(id+"F7.boolean.opBoolean","SPLIT",EDGE,{"disambiguationData":[TD([makeQuery(id+"F7.opExtrude","SWEPT_FACE",FACE,{"disambiguationData":[OSD([sQuery(id+"F6.wireOp",EDGE,"E10.1.0.0")])]})])],"derivedFrom":makeQuery(id+"F3.opExtrude","CAP_EDGE",EDGE,{"disambiguationData":[OSD([subQ0])],"isStart":false})});}
            var Q29;
            Q29=makeQuery(id+"F12.boolean.opBoolean","INTERSECT",EDGE,{"derivedFrom":[makeQuery(id+"F7.boolean.opBoolean","COPY",FACE,{"derivedFrom":makeQuery(id+"F7.opExtrude","SWEPT_FACE",FACE,{"disambiguationData":[OSD([sQuery(id+"F6.wireOp",EDGE,"E10.1.0.1")])]})}),makeQuery(id+"F12.opExtrude","SWEPT_FACE",FACE,{"disambiguationData":[OSD([sQuery(id+"F11.wireOp",EDGE,"E48.trimOffspring")])]})]});
            var Q30;
            {var subQ0=sQuery(id+"F2.wireOp",EDGE,"E5.left");Q30=makeQuery(id+"F7.boolean.opBoolean","SPLIT",EDGE,{"disambiguationData":[TD([makeQuery(id+"F7.opExtrude","SWEPT_FACE",FACE,{"disambiguationData":[OSD([sQuery(id+"F6.wireOp",EDGE,"E9")])]})])],"derivedFrom":makeQuery(id+"F3.opExtrude","CAP_EDGE",EDGE,{"disambiguationData":[OSD([subQ0])],"isStart":false})});}
            var Q31;
            Q31=makeQuery(id+"F12.boolean.opBoolean","INTERSECT",EDGE,{"derivedFrom":[makeQuery(id+"F7.boolean.opBoolean","COPY",FACE,{"derivedFrom":makeQuery(id+"F7.opExtrude","SWEPT_FACE",FACE,{"disambiguationData":[OSD([sQuery(id+"F6.wireOp",EDGE,"E8")])]})}),makeQuery(id+"F12.opExtrude","SWEPT_FACE",FACE,{"disambiguationData":[OSD([sQuery(id+"F11.wireOp",EDGE,"E44.trimOffspring")])]})]});
            var Q32;
            {var subQ0=sQuery(id+"F2.wireOp",EDGE,"E5.left");var subQ1=sQuery(id+"F2.wireOp",EDGE,"E5.top");Q32=makeQuery(id+"F7.boolean.opBoolean","SPLIT",EDGE,{"disambiguationData":[TD([makeQuery(id+"F3.opExtrude","SWEPT_FACE",FACE,{"disambiguationData":[OSD([subQ1])]})])],"derivedFrom":makeQuery(id+"F3.opExtrude","CAP_EDGE",EDGE,{"disambiguationData":[OSD([subQ0])],"isStart":false})});}
            var Q33;
            {var subQ0=sQuery(id+"F2.wireOp",EDGE,"E5.left");var subQ1=sQuery(id+"F2.wireOp",EDGE,"E5.top");Q33=makeQuery(id+"F7.boolean.opBoolean","SPLIT",EDGE,{"disambiguationData":[TD([makeQuery(id+"F3.opExtrude","SWEPT_FACE",FACE,{"disambiguationData":[OSD([subQ1])]})])],"derivedFrom":makeQuery(id+"F3.opExtrude","CAP_EDGE",EDGE,{"disambiguationData":[OSD([subQ0])],"isStart":true})});}
            var Q34;
            Q34=makeQuery(id+"F12.boolean.opBoolean","INTERSECT",EDGE,{"derivedFrom":[makeQuery(id+"F7.boolean.opBoolean","COPY",FACE,{"derivedFrom":makeQuery(id+"F7.opExtrude","SWEPT_FACE",FACE,{"disambiguationData":[OSD([sQuery(id+"F6.wireOp",EDGE,"E28.MirrorCS")])]})}),makeQuery(id+"F12.opExtrude","SWEPT_FACE",FACE,{"disambiguationData":[OSD([sQuery(id+"F11.wireOp",EDGE,"E44.trimOffspring")])]})]});
            var Q35;
            {var subQ0=sQuery(id+"F2.wireOp",EDGE,"E5.left");Q35=makeQuery(id+"F7.boolean.opBoolean","SPLIT",EDGE,{"disambiguationData":[TD([makeQuery(id+"F7.opExtrude","SWEPT_FACE",FACE,{"disambiguationData":[OSD([sQuery(id+"F6.wireOp",EDGE,"E20.MirrorCS")])]})])],"derivedFrom":makeQuery(id+"F3.opExtrude","CAP_EDGE",EDGE,{"disambiguationData":[OSD([subQ0])],"isStart":true})});}
            var Q36;
            Q36=makeQuery(id+"F12.boolean.opBoolean","INTERSECT",EDGE,{"derivedFrom":[makeQuery(id+"F7.boolean.opBoolean","COPY",FACE,{"derivedFrom":makeQuery(id+"F7.opExtrude","SWEPT_FACE",FACE,{"disambiguationData":[OSD([sQuery(id+"F6.wireOp",EDGE,"E36.MirrorCS")])]})}),makeQuery(id+"F12.opExtrude","SWEPT_FACE",FACE,{"disambiguationData":[OSD([sQuery(id+"F11.wireOp",EDGE,"E48.trimOffspring")])]})]});
            var Q37;
            {var subQ0=sQuery(id+"F2.wireOp",EDGE,"E5.left");Q37=makeQuery(id+"F7.boolean.opBoolean","SPLIT",EDGE,{"disambiguationData":[TD([makeQuery(id+"F7.opExtrude","SWEPT_FACE",FACE,{"disambiguationData":[OSD([sQuery(id+"F6.wireOp",EDGE,"E21.MirrorCS")])]})])],"derivedFrom":makeQuery(id+"F3.opExtrude","CAP_EDGE",EDGE,{"disambiguationData":[OSD([subQ0])],"isStart":true})});}
            var Q38;
            Q38=makeQuery(id+"F12.boolean.opBoolean","INTERSECT",EDGE,{"derivedFrom":[makeQuery(id+"F7.boolean.opBoolean","COPY",FACE,{"derivedFrom":makeQuery(id+"F7.opExtrude","SWEPT_FACE",FACE,{"disambiguationData":[OSD([sQuery(id+"F6.wireOp",EDGE,"E37.MirrorCS")])]})}),makeQuery(id+"F12.opExtrude","SWEPT_FACE",FACE,{"disambiguationData":[OSD([sQuery(id+"F11.wireOp",EDGE,"E51.trimOffspring")])]})]});
            var Q39;
            {var subQ0=sQuery(id+"F2.wireOp",EDGE,"E5.left");Q39=makeQuery(id+"F7.boolean.opBoolean","SPLIT",EDGE,{"disambiguationData":[TD([makeQuery(id+"F7.opExtrude","SWEPT_FACE",FACE,{"disambiguationData":[OSD([sQuery(id+"F6.wireOp",EDGE,"E18.MirrorCS")])]})])],"derivedFrom":makeQuery(id+"F3.opExtrude","CAP_EDGE",EDGE,{"disambiguationData":[OSD([subQ0])],"isStart":true})});}
            var Q40;
            Q40=makeQuery(id+"F12.boolean.opBoolean","INTERSECT",EDGE,{"derivedFrom":[makeQuery(id+"F7.boolean.opBoolean","COPY",FACE,{"derivedFrom":makeQuery(id+"F7.opExtrude","SWEPT_FACE",FACE,{"disambiguationData":[OSD([sQuery(id+"F6.wireOp",EDGE,"E29.MirrorCS")])]})}),makeQuery(id+"F12.opExtrude","SWEPT_FACE",FACE,{"disambiguationData":[OSD([sQuery(id+"F11.wireOp",EDGE,"E54.trimOffspring")])]})]});
            var Q41;
            {var subQ0=sQuery(id+"F2.wireOp",EDGE,"E5.left");Q41=makeQuery(id+"F7.boolean.opBoolean","SPLIT",EDGE,{"disambiguationData":[TD([makeQuery(id+"F7.opExtrude","SWEPT_FACE",FACE,{"disambiguationData":[OSD([sQuery(id+"F6.wireOp",EDGE,"E25.MirrorCS")])]})])],"derivedFrom":makeQuery(id+"F3.opExtrude","CAP_EDGE",EDGE,{"disambiguationData":[OSD([subQ0])],"isStart":true})});}
            var Q42;
            Q42=makeQuery(id+"F12.boolean.opBoolean","INTERSECT",EDGE,{"derivedFrom":[makeQuery(id+"F7.boolean.opBoolean","COPY",FACE,{"derivedFrom":makeQuery(id+"F7.opExtrude","SWEPT_FACE",FACE,{"disambiguationData":[OSD([sQuery(id+"F6.wireOp",EDGE,"E33.MirrorCS")])]})}),makeQuery(id+"F12.opExtrude","SWEPT_FACE",FACE,{"disambiguationData":[OSD([sQuery(id+"F11.wireOp",EDGE,"E41")])]})]});
            var Q43;
            {var subQ0=sQuery(id+"F2.wireOp",EDGE,"E5.bottom");var subQ1=sQuery(id+"F2.wireOp",EDGE,"E5.left");Q43=makeQuery(id+"F7.boolean.opBoolean","SPLIT",EDGE,{"disambiguationData":[TD([makeQuery(id+"F3.opExtrude","SWEPT_FACE",FACE,{"disambiguationData":[OSD([subQ0])]})])],"derivedFrom":makeQuery(id+"F3.opExtrude","CAP_EDGE",EDGE,{"disambiguationData":[OSD([subQ1])],"isStart":true})});}
            fillet(context, id + "F21", {"entities" : qUnion([Q0, Q1, Q2, Q3, Q4, Q5, Q6, Q7, Q8, Q9, Q10, Q11, Q12, Q13, Q14, Q15, Q16, Q17, Q18, Q19, Q20, Q21, Q22, Q23, Q24, Q25, Q26, Q27, Q28, Q29, Q30, Q31, Q32, Q33, Q34, Q35, Q36, Q37, Q38, Q39, Q40, Q41, Q42, Q43]), "radius" : 5 * mm, "tangentPropagation" : true, "allowEdgeOverflow" : false});
        }
        {
            var Q0;
            Q0=makeQuery(id+"F1.opExtrude","SWEPT_FACE",FACE,{"disambiguationData":[OSD([sQuery(id+"F0.wireOp",EDGE,"E0.top")])]});
            var sketch = newSketch(context, id + "F22", { "sketchPlane" : qUnion([Q0])});
            skLineSegment(sketch, "E104.0", {"start": v(-480.5, 10) * mm, "end": v(-478.5, 10) * mm});
            skLineSegment(sketch, "E104.1", {"start": v(-480.5, 18) * mm, "end": v(-478.5, 18) * mm});
            skLineSegment(sketch, "E104.2", {"start": v(-480.5, 28) * mm, "end": v(-478.5, 28) * mm});
            skLineSegment(sketch, "E104.3", {"start": v(-480.5, 36) * mm, "end": v(-478.5, 36) * mm});
            skLineSegment(sketch, "E104.4", {"start": v(-480.5, 46) * mm, "end": v(-478.5, 46) * mm});
            skLineSegment(sketch, "E104.5", {"start": v(-480.5, 54) * mm, "end": v(-478.5, 54) * mm});
            skLineSegment(sketch, "E104.6", {"start": v(-480.5, 64) * mm, "end": v(-478.5, 64) * mm});
            skLineSegment(sketch, "E104.7", {"start": v(-480.5, 72) * mm, "end": v(-478.5, 72) * mm});
            skLineSegment(sketch, "E105.0", {"start": v(-480.5, 90) * mm, "end": v(-480.5, 82) * mm});
            skLineSegment(sketch, "E106.0", {"start": v(-478.5, 90) * mm, "end": v(-478.5, 82) * mm});
            skPoint(sketch, "E107.orphan", {"position": v(-480.5, 0) * mm});
            skPoint(sketch, "E108.orphan", {"position": v(745, 10) * mm});
            skPoint(sketch, "E109.orphan", {"position": v(745, 18) * mm});
            skPoint(sketch, "E110.orphan", {"position": v(745, 28) * mm});
            skPoint(sketch, "E111.orphan", {"position": v(745, 46) * mm});
            skPoint(sketch, "E112.orphan", {"position": v(745, 36) * mm});
            skPoint(sketch, "E113.orphan", {"position": v(745, 54) * mm});
            skPoint(sketch, "E114.orphan", {"position": v(745, 64) * mm});
            skPoint(sketch, "E115.orphan", {"position": v(745, 72) * mm});
            skPoint(sketch, "E116.orphan", {"position": v(-745, 72) * mm});
            skPoint(sketch, "E117.orphan", {"position": v(-745, 64) * mm});
            skPoint(sketch, "E118.orphan", {"position": v(-745, 54) * mm});
            skPoint(sketch, "E119.orphan", {"position": v(-745, 46) * mm});
            skPoint(sketch, "E120.orphan", {"position": v(-745, 36) * mm});
            skPoint(sketch, "E121.orphan", {"position": v(-745, 28) * mm});
            skPoint(sketch, "E122.orphan", {"position": v(-745, 18) * mm});
            skPoint(sketch, "E123.orphan", {"position": v(-745, 10) * mm});
            skLineSegment(sketch, "E124.trimOffspring", {"start": v(-478.5, 18) * mm, "end": v(-478.5, 10) * mm});
            skLineSegment(sketch, "E125.trimOffspring", {"start": v(-480.5, 18) * mm, "end": v(-480.5, 10) * mm});
            skLineSegment(sketch, "E126.trimOffspring", {"start": v(-478.5, 36) * mm, "end": v(-478.5, 28) * mm});
            skLineSegment(sketch, "E127.trimOffspring", {"start": v(-480.5, 36) * mm, "end": v(-480.5, 28) * mm});
            skLineSegment(sketch, "E128", {"start": v(-480.5, 82) * mm, "end": v(-478.5, 82) * mm});
            skLineSegment(sketch, "E129", {"start": v(-478.5, 82) * mm, "end": v(-478.5, 90) * mm});
            skLineSegment(sketch, "E130", {"start": v(-478.5, 90) * mm, "end": v(-480.5, 90) * mm});
            skLineSegment(sketch, "E131.trimOffspring", {"start": v(-480.5, 54) * mm, "end": v(-480.5, 46) * mm});
            skLineSegment(sketch, "E132.trimOffspring", {"start": v(-478.5, 54) * mm, "end": v(-478.5, 46) * mm});
            skLineSegment(sketch, "E133.trimOffspring", {"start": v(-480.5, 72) * mm, "end": v(-480.5, 64) * mm});
            skLineSegment(sketch, "E134.trimOffspring", {"start": v(-478.5, 72) * mm, "end": v(-478.5, 64) * mm});
            skPoint(sketch, "E135.orphan", {"position": v(-480.5, 100) * mm});
            skLineSegment(sketch, "E136.MirrorCS", {"start": v(478.5, 82) * mm, "end": v(478.5, 90) * mm});
            skLineSegment(sketch, "E137.MirrorCS", {"start": v(480.5, 82) * mm, "end": v(478.5, 82) * mm});
            skLineSegment(sketch, "E138.MirrorCS", {"start": v(480.5, 10) * mm, "end": v(478.5, 10) * mm});
            skLineSegment(sketch, "E139.MirrorCS", {"start": v(478.5, 90) * mm, "end": v(480.5, 90) * mm});
            skLineSegment(sketch, "E140.MirrorCS", {"start": v(480.5, 18) * mm, "end": v(478.5, 18) * mm});
            skLineSegment(sketch, "E141.MirrorCS", {"start": v(478.5, 90) * mm, "end": v(478.5, 82) * mm});
            skLineSegment(sketch, "E142.MirrorCS", {"start": v(480.5, 90) * mm, "end": v(480.5, 82) * mm});
            skLineSegment(sketch, "E143.MirrorCS", {"start": v(480.5, 54) * mm, "end": v(480.5, 46) * mm});
            skLineSegment(sketch, "E144.MirrorCS", {"start": v(478.5, 72) * mm, "end": v(478.5, 64) * mm});
            skLineSegment(sketch, "E145.MirrorCS", {"start": v(480.5, 36) * mm, "end": v(480.5, 28) * mm});
            skLineSegment(sketch, "E146.MirrorCS", {"start": v(478.5, 36) * mm, "end": v(478.5, 28) * mm});
            skLineSegment(sketch, "E147.MirrorCS", {"start": v(480.5, 18) * mm, "end": v(480.5, 10) * mm});
            skLineSegment(sketch, "E148.MirrorCS", {"start": v(480.5, 72) * mm, "end": v(480.5, 64) * mm});
            skLineSegment(sketch, "E149.MirrorCS", {"start": v(478.5, 18) * mm, "end": v(478.5, 10) * mm});
            skLineSegment(sketch, "E150.MirrorCS", {"start": v(480.5, 28) * mm, "end": v(478.5, 28) * mm});
            skLineSegment(sketch, "E151.MirrorCS", {"start": v(478.5, 54) * mm, "end": v(478.5, 46) * mm});
            skLineSegment(sketch, "E152.MirrorCS", {"start": v(480.5, 72) * mm, "end": v(478.5, 72) * mm});
            skLineSegment(sketch, "E153.MirrorCS", {"start": v(480.5, 64) * mm, "end": v(478.5, 64) * mm});
            skLineSegment(sketch, "E154.MirrorCS", {"start": v(480.5, 54) * mm, "end": v(478.5, 54) * mm});
            skLineSegment(sketch, "E155.MirrorCS", {"start": v(480.5, 46) * mm, "end": v(478.5, 46) * mm});
            skLineSegment(sketch, "E156.MirrorCS", {"start": v(480.5, 36) * mm, "end": v(478.5, 36) * mm});
            skPoint(sketch, "E157.MirrorP", {"position": v(480.5, 100) * mm});
            skPoint(sketch, "E158.MirrorP", {"position": v(480.5, 0) * mm});
            skSolve(sketch);
        }
        {
            var Q0;
            Q0 = qSketchRegion(id + "F22", true);
            extrude(context, id + "F23", {"entities" : qUnion([Q0]), "operationType" : NewBodyOperationType.REMOVE, "endBound" : BoundingType.THROUGH_ALL, "oppositeDirection" : true, "depth" : 25 * mm, "offsetDistance" : 25 * mm});
        }
        {
            var Q0;
            Q0=makeQuery(id+"F1.opExtrude","SWEPT_FACE",FACE,{"disambiguationData":[OSD([sQuery(id+"F0.wireOp",EDGE,"E0.top")])]});
            var sketch = newSketch(context, id + "F24", { "sketchPlane" : qUnion([Q0])});
            skLineSegment(sketch, "E159.0", {"start": v(-432.5, 90) * mm, "end": v(-432.5, 82) * mm});
            skPoint(sketch, "E160.0", {"position": v(-430.5, 90) * mm});
            skPoint(sketch, "E160.1", {"position": v(-430.5, 82) * mm});
            skPoint(sketch, "E160.2", {"position": v(-430.5, 72) * mm});
            skPoint(sketch, "E160.3", {"position": v(-430.5, 64) * mm});
            skPoint(sketch, "E160.4", {"position": v(-430.5, 54) * mm});
            skPoint(sketch, "E160.5", {"position": v(-430.5, 46) * mm});
            skPoint(sketch, "E160.6", {"position": v(-430.5, 36) * mm});
            skPoint(sketch, "E160.7", {"position": v(-430.5, 28) * mm});
            skPoint(sketch, "E160.8", {"position": v(-430.5, 18) * mm});
            skPoint(sketch, "E160.9", {"position": v(-430.5, 10) * mm});
            skLineSegment(sketch, "E161", {"start": v(-430.5, 10) * mm, "end": v(-432.5, 10) * mm});
            skLineSegment(sketch, "E162", {"start": v(-430.5, 10) * mm, "end": v(-430.5, 18) * mm});
            skLineSegment(sketch, "E163", {"start": v(-430.5, 18) * mm, "end": v(-432.5, 18) * mm});
            skLineSegment(sketch, "E164", {"start": v(-432.5, 28) * mm, "end": v(-430.5, 28) * mm});
            skLineSegment(sketch, "E165", {"start": v(-430.5, 28) * mm, "end": v(-430.5, 36) * mm});
            skLineSegment(sketch, "E166", {"start": v(-432.5, 36) * mm, "end": v(-430.5, 36) * mm});
            skLineSegment(sketch, "E167", {"start": v(-430.5, 46) * mm, "end": v(-432.5, 46) * mm});
            skLineSegment(sketch, "E168", {"start": v(-430.5, 46) * mm, "end": v(-430.5, 54) * mm});
            skLineSegment(sketch, "E169", {"start": v(-432.5, 54) * mm, "end": v(-430.5, 54) * mm});
            skLineSegment(sketch, "E170", {"start": v(-432.5, 64) * mm, "end": v(-430.5, 64) * mm});
            skLineSegment(sketch, "E171", {"start": v(-430.5, 64) * mm, "end": v(-430.5, 72) * mm});
            skLineSegment(sketch, "E172", {"start": v(-432.5, 72) * mm, "end": v(-430.5, 72) * mm});
            skLineSegment(sketch, "E173", {"start": v(-432.5, 82) * mm, "end": v(-430.5, 82) * mm});
            skLineSegment(sketch, "E174", {"start": v(-430.5, 82) * mm, "end": v(-430.5, 90) * mm});
            skLineSegment(sketch, "E175", {"start": v(-432.5, 90) * mm, "end": v(-430.5, 90) * mm});
            skLineSegment(sketch, "E176.trimOffspring", {"start": v(-432.5, 72) * mm, "end": v(-432.5, 64) * mm});
            skLineSegment(sketch, "E177.trimOffspring", {"start": v(-432.5, 54) * mm, "end": v(-432.5, 46) * mm});
            skLineSegment(sketch, "E178.trimOffspring", {"start": v(-432.5, 36) * mm, "end": v(-432.5, 28) * mm});
            skLineSegment(sketch, "E179.trimOffspring", {"start": v(-432.5, 18) * mm, "end": v(-432.5, 10) * mm});
            skSolve(sketch);
        }
        {
            var Q0;
            Q0 = qSketchRegion(id + "F24", true);
            var Q1;
            Q1=makeQuery(id+"F1.opExtrude","CAP_EDGE",EDGE,{"disambiguationData":[OSD([sQuery(id+"F0.wireOp",EDGE,"E0.right")])],"isStart":false});
            var Q2;
            Q2=makeQuery(id+"F14.opExtrude","CAP_EDGE",EDGE,{"disambiguationData":[OSD([sQuery(id+"F13.wireOp",EDGE,"E76.top")])],"isStart":false});
            var Q3;
            Q3=makeQuery(id+"F1.opExtrude","CAP_EDGE",EDGE,{"disambiguationData":[OSD([sQuery(id+"F0.wireOp",EDGE,"E2.MirrorCS")])],"isStart":false});
            sweep(context, id + "F25", {"operationType" : NewBodyOperationType.REMOVE, "profiles" : qUnion([Q0]), "path" : qUnion([Q1, Q2, Q3])});
        }
        {
            var Q0;
            {var subQ0=sQuery(id+"F2.wireOp",EDGE,"jYso9TrC-VrG6-bpdd-wlHX-91mLgS95FXrc.right");var subQ1=sQuery(id+"F2.wireOp",EDGE,"jYso9TrC-VrG6-bpdd-wlHX-91mLgS95FXrc.top");Q0=makeQuery(id+"F7.boolean.opBoolean","SPLIT",EDGE,{"disambiguationData":[TD([makeQuery(id+"F3.opExtrude","SWEPT_FACE",FACE,{"disambiguationData":[OSD([subQ1])]})])],"derivedFrom":makeQuery(id+"F3.opExtrude","CAP_EDGE",EDGE,{"disambiguationData":[OSD([subQ0])],"isStart":true})});}
            var Q1;
            {var subQ0=sQuery(id+"F2.wireOp",EDGE,"jYso9TrC-VrG6-bpdd-wlHX-91mLgS95FXrc.right");Q1=makeQuery(id+"F7.boolean.opBoolean","SPLIT",EDGE,{"disambiguationData":[TD([makeQuery(id+"F7.opExtrude","SWEPT_FACE",FACE,{"disambiguationData":[OSD([sQuery(id+"F6.wireOp",EDGE,"E9")])]})])],"derivedFrom":makeQuery(id+"F3.opExtrude","CAP_EDGE",EDGE,{"disambiguationData":[OSD([subQ0])],"isStart":true})});}
            var Q2;
            {var subQ0=sQuery(id+"F2.wireOp",EDGE,"jYso9TrC-VrG6-bpdd-wlHX-91mLgS95FXrc.right");Q2=makeQuery(id+"F7.boolean.opBoolean","SPLIT",EDGE,{"disambiguationData":[TD([makeQuery(id+"F7.opExtrude","SWEPT_FACE",FACE,{"disambiguationData":[OSD([sQuery(id+"F6.wireOp",EDGE,"E10.1.0.0")])]})])],"derivedFrom":makeQuery(id+"F3.opExtrude","CAP_EDGE",EDGE,{"disambiguationData":[OSD([subQ0])],"isStart":true})});}
            var Q3;
            {var subQ0=sQuery(id+"F2.wireOp",EDGE,"jYso9TrC-VrG6-bpdd-wlHX-91mLgS95FXrc.right");Q3=makeQuery(id+"F7.boolean.opBoolean","SPLIT",EDGE,{"disambiguationData":[TD([makeQuery(id+"F7.opExtrude","SWEPT_FACE",FACE,{"disambiguationData":[OSD([sQuery(id+"F6.wireOp",EDGE,"E10.2.0.0")])]})])],"derivedFrom":makeQuery(id+"F3.opExtrude","CAP_EDGE",EDGE,{"disambiguationData":[OSD([subQ0])],"isStart":true})});}
            var Q4;
            {var subQ0=sQuery(id+"F2.wireOp",EDGE,"jYso9TrC-VrG6-bpdd-wlHX-91mLgS95FXrc.right");Q4=makeQuery(id+"F7.boolean.opBoolean","SPLIT",EDGE,{"disambiguationData":[TD([makeQuery(id+"F7.opExtrude","SWEPT_FACE",FACE,{"disambiguationData":[OSD([sQuery(id+"F6.wireOp",EDGE,"E10.3.0.0")])]})])],"derivedFrom":makeQuery(id+"F3.opExtrude","CAP_EDGE",EDGE,{"disambiguationData":[OSD([subQ0])],"isStart":true})});}
            var Q5;
            {var subQ0=sQuery(id+"F2.wireOp",EDGE,"jYso9TrC-VrG6-bpdd-wlHX-91mLgS95FXrc.bottom");var subQ1=sQuery(id+"F2.wireOp",EDGE,"jYso9TrC-VrG6-bpdd-wlHX-91mLgS95FXrc.right");Q5=makeQuery(id+"F7.boolean.opBoolean","SPLIT",EDGE,{"disambiguationData":[TD([makeQuery(id+"F3.opExtrude","SWEPT_FACE",FACE,{"disambiguationData":[OSD([subQ0])]})])],"derivedFrom":makeQuery(id+"F3.opExtrude","CAP_EDGE",EDGE,{"disambiguationData":[OSD([subQ1])],"isStart":true})});}
            var Q6;
            Q6=makeQuery(id+"Fou14xSP3GQJlB0_5.boolean.opBoolean","INTERSECT",EDGE,{"derivedFrom":[makeQuery(id+"F7.boolean.opBoolean","COPY",FACE,{"disambiguationData":[TD([makeQuery(id+"F3.opExtrude","SWEPT_FACE",FACE,{"disambiguationData":[OSD([sQuery(id+"F2.wireOp",EDGE,"jYso9TrC-VrG6-bpdd-wlHX-91mLgS95FXrc.left")])]})])],"derivedFrom":makeQuery(id+"F7.opExtrude","SWEPT_FACE",FACE,{"disambiguationData":[OSD([sQuery(id+"F6.wireOp",EDGE,"E10.4.0.1")])]})}),makeQuery(id+"Fou14xSP3GQJlB0_5.opExtrude","SWEPT_FACE",FACE,{"disambiguationData":[OSD([sQuery(id+"Ffmn4ZGQaAwYWcj_5.wireOp",EDGE,"a3c56a51-e62f-46ba-aa57-5dfe259011c510.MirrorCS")])]})]});
            var Q7;
            Q7=makeQuery(id+"Fou14xSP3GQJlB0_5.boolean.opBoolean","INTERSECT",EDGE,{"derivedFrom":[makeQuery(id+"F7.boolean.opBoolean","COPY",FACE,{"disambiguationData":[TD([makeQuery(id+"F3.opExtrude","SWEPT_FACE",FACE,{"disambiguationData":[OSD([sQuery(id+"F2.wireOp",EDGE,"jYso9TrC-VrG6-bpdd-wlHX-91mLgS95FXrc.left")])]})])],"derivedFrom":makeQuery(id+"F7.opExtrude","SWEPT_FACE",FACE,{"disambiguationData":[OSD([sQuery(id+"F6.wireOp",EDGE,"E10.3.0.1")])]})}),makeQuery(id+"Fou14xSP3GQJlB0_5.opExtrude","SWEPT_FACE",FACE,{"disambiguationData":[OSD([sQuery(id+"Ffmn4ZGQaAwYWcj_5.wireOp",EDGE,"a3c56a51-e62f-46ba-aa57-5dfe259011c59.MirrorCS")])]})]});
            var Q8;
            Q8=makeQuery(id+"Fou14xSP3GQJlB0_5.boolean.opBoolean","INTERSECT",EDGE,{"derivedFrom":[makeQuery(id+"F7.boolean.opBoolean","COPY",FACE,{"disambiguationData":[TD([makeQuery(id+"F3.opExtrude","SWEPT_FACE",FACE,{"disambiguationData":[OSD([sQuery(id+"F2.wireOp",EDGE,"jYso9TrC-VrG6-bpdd-wlHX-91mLgS95FXrc.left")])]})])],"derivedFrom":makeQuery(id+"F7.opExtrude","SWEPT_FACE",FACE,{"disambiguationData":[OSD([sQuery(id+"F6.wireOp",EDGE,"E10.2.0.1")])]})}),makeQuery(id+"Fou14xSP3GQJlB0_5.opExtrude","SWEPT_FACE",FACE,{"disambiguationData":[OSD([sQuery(id+"Ffmn4ZGQaAwYWcj_5.wireOp",EDGE,"a3c56a51-e62f-46ba-aa57-5dfe259011c58.MirrorCS")])]})]});
            var Q9;
            Q9=makeQuery(id+"Fou14xSP3GQJlB0_5.boolean.opBoolean","INTERSECT",EDGE,{"derivedFrom":[makeQuery(id+"F7.boolean.opBoolean","COPY",FACE,{"disambiguationData":[TD([makeQuery(id+"F3.opExtrude","SWEPT_FACE",FACE,{"disambiguationData":[OSD([sQuery(id+"F2.wireOp",EDGE,"jYso9TrC-VrG6-bpdd-wlHX-91mLgS95FXrc.left")])]})])],"derivedFrom":makeQuery(id+"F7.opExtrude","SWEPT_FACE",FACE,{"disambiguationData":[OSD([sQuery(id+"F6.wireOp",EDGE,"E10.1.0.1")])]})}),makeQuery(id+"Fou14xSP3GQJlB0_5.opExtrude","SWEPT_FACE",FACE,{"disambiguationData":[OSD([sQuery(id+"Ffmn4ZGQaAwYWcj_5.wireOp",EDGE,"a3c56a51-e62f-46ba-aa57-5dfe259011c520.MirrorCS")])]})]});
            var Q10;
            Q10=makeQuery(id+"Fou14xSP3GQJlB0_5.boolean.opBoolean","INTERSECT",EDGE,{"derivedFrom":[makeQuery(id+"F7.boolean.opBoolean","COPY",FACE,{"disambiguationData":[TD([makeQuery(id+"F3.opExtrude","SWEPT_FACE",FACE,{"disambiguationData":[OSD([sQuery(id+"F2.wireOp",EDGE,"jYso9TrC-VrG6-bpdd-wlHX-91mLgS95FXrc.left")])]})])],"derivedFrom":makeQuery(id+"F7.opExtrude","SWEPT_FACE",FACE,{"disambiguationData":[OSD([sQuery(id+"F6.wireOp",EDGE,"E8")])]})}),makeQuery(id+"Fou14xSP3GQJlB0_5.opExtrude","SWEPT_FACE",FACE,{"disambiguationData":[OSD([sQuery(id+"Ffmn4ZGQaAwYWcj_5.wireOp",EDGE,"a3c56a51-e62f-46ba-aa57-5dfe259011c518.MirrorCS")])]})]});
            var Q11;
            {var subQ0=sQuery(id+"F2.wireOp",EDGE,"jYso9TrC-VrG6-bpdd-wlHX-91mLgS95FXrc.left");var subQ1=sQuery(id+"F2.wireOp",EDGE,"jYso9TrC-VrG6-bpdd-wlHX-91mLgS95FXrc.top");Q11=makeQuery(id+"F7.boolean.opBoolean","SPLIT",EDGE,{"disambiguationData":[TD([makeQuery(id+"F3.opExtrude","SWEPT_FACE",FACE,{"disambiguationData":[OSD([subQ1])]})])],"derivedFrom":makeQuery(id+"F3.opExtrude","CAP_EDGE",EDGE,{"disambiguationData":[OSD([subQ0])],"isStart":true})});}
            var Q12;
            {var subQ0=sQuery(id+"F2.wireOp",EDGE,"jYso9TrC-VrG6-bpdd-wlHX-91mLgS95FXrc.left");Q12=makeQuery(id+"F7.boolean.opBoolean","SPLIT",EDGE,{"disambiguationData":[TD([makeQuery(id+"F7.opExtrude","SWEPT_FACE",FACE,{"disambiguationData":[OSD([sQuery(id+"F6.wireOp",EDGE,"E9")])]})])],"derivedFrom":makeQuery(id+"F3.opExtrude","CAP_EDGE",EDGE,{"disambiguationData":[OSD([subQ0])],"isStart":true})});}
            var Q13;
            {var subQ0=sQuery(id+"F2.wireOp",EDGE,"jYso9TrC-VrG6-bpdd-wlHX-91mLgS95FXrc.left");Q13=makeQuery(id+"F7.boolean.opBoolean","SPLIT",EDGE,{"disambiguationData":[TD([makeQuery(id+"F7.opExtrude","SWEPT_FACE",FACE,{"disambiguationData":[OSD([sQuery(id+"F6.wireOp",EDGE,"E10.1.0.0")])]})])],"derivedFrom":makeQuery(id+"F3.opExtrude","CAP_EDGE",EDGE,{"disambiguationData":[OSD([subQ0])],"isStart":true})});}
            var Q14;
            {var subQ0=sQuery(id+"F2.wireOp",EDGE,"jYso9TrC-VrG6-bpdd-wlHX-91mLgS95FXrc.left");Q14=makeQuery(id+"F7.boolean.opBoolean","SPLIT",EDGE,{"disambiguationData":[TD([makeQuery(id+"F7.opExtrude","SWEPT_FACE",FACE,{"disambiguationData":[OSD([sQuery(id+"F6.wireOp",EDGE,"E10.2.0.0")])]})])],"derivedFrom":makeQuery(id+"F3.opExtrude","CAP_EDGE",EDGE,{"disambiguationData":[OSD([subQ0])],"isStart":true})});}
            var Q15;
            {var subQ0=sQuery(id+"F2.wireOp",EDGE,"jYso9TrC-VrG6-bpdd-wlHX-91mLgS95FXrc.bottom");var subQ1=sQuery(id+"F2.wireOp",EDGE,"jYso9TrC-VrG6-bpdd-wlHX-91mLgS95FXrc.left");Q15=makeQuery(id+"F7.boolean.opBoolean","SPLIT",EDGE,{"disambiguationData":[TD([makeQuery(id+"F3.opExtrude","SWEPT_FACE",FACE,{"disambiguationData":[OSD([subQ0])]})])],"derivedFrom":makeQuery(id+"F3.opExtrude","CAP_EDGE",EDGE,{"disambiguationData":[OSD([subQ1])],"isStart":true})});}
            var Q16;
            Q16=makeQuery(id+"F1.opExtrude","SWEPT_EDGE",EDGE,{"disambiguationData":[OSD([sQuery(id+"F0.wireOp",EDGE,"E3.MirrorCS"),sQuery(id+"F0.wireOp",EDGE,"E4.MirrorCS")])]});
            var Q17;
            {var subQ0=sQuery(id+"F2.wireOp",EDGE,"jYso9TrC-VrG6-bpdd-wlHX-91mLgS95FXrc.left");Q17=makeQuery(id+"F7.boolean.opBoolean","SPLIT",EDGE,{"disambiguationData":[TD([makeQuery(id+"F7.opExtrude","SWEPT_FACE",FACE,{"disambiguationData":[OSD([sQuery(id+"F6.wireOp",EDGE,"E10.3.0.0")])]})])],"derivedFrom":makeQuery(id+"F3.opExtrude","CAP_EDGE",EDGE,{"disambiguationData":[OSD([subQ0])],"isStart":true})});}
            var Q18;
            Q18=makeQuery(id+"F7.boolean.opBoolean","INTERSECT",EDGE,{"derivedFrom":[makeQuery(id+"F3.opExtrude","SWEPT_FACE",FACE,{"disambiguationData":[OSD([sQuery(id+"F2.wireOp",EDGE,"jYso9TrC-VrG6-bpdd-wlHX-91mLgS95FXrc.left")])]}),makeQuery(id+"F7.opExtrude","SWEPT_FACE",FACE,{"disambiguationData":[OSD([sQuery(id+"F6.wireOp",EDGE,"E10.4.0.1")])]})]});
            var Q19;
            Q19=makeQuery(id+"F7.boolean.opBoolean","INTERSECT",EDGE,{"derivedFrom":[makeQuery(id+"F3.opExtrude","SWEPT_FACE",FACE,{"disambiguationData":[OSD([sQuery(id+"F2.wireOp",EDGE,"jYso9TrC-VrG6-bpdd-wlHX-91mLgS95FXrc.left")])]}),makeQuery(id+"F7.opExtrude","SWEPT_FACE",FACE,{"disambiguationData":[OSD([sQuery(id+"F6.wireOp",EDGE,"E10.3.0.1")])]})]});
            var Q20;
            Q20=makeQuery(id+"F7.boolean.opBoolean","INTERSECT",EDGE,{"derivedFrom":[makeQuery(id+"F3.opExtrude","SWEPT_FACE",FACE,{"disambiguationData":[OSD([sQuery(id+"F2.wireOp",EDGE,"jYso9TrC-VrG6-bpdd-wlHX-91mLgS95FXrc.left")])]}),makeQuery(id+"F7.opExtrude","SWEPT_FACE",FACE,{"disambiguationData":[OSD([sQuery(id+"F6.wireOp",EDGE,"E10.2.0.1")])]})]});
            var Q21;
            Q21=makeQuery(id+"F7.boolean.opBoolean","INTERSECT",EDGE,{"derivedFrom":[makeQuery(id+"F3.opExtrude","SWEPT_FACE",FACE,{"disambiguationData":[OSD([sQuery(id+"F2.wireOp",EDGE,"jYso9TrC-VrG6-bpdd-wlHX-91mLgS95FXrc.left")])]}),makeQuery(id+"F7.opExtrude","SWEPT_FACE",FACE,{"disambiguationData":[OSD([sQuery(id+"F6.wireOp",EDGE,"E10.1.0.1")])]})]});
            var Q22;
            Q22=makeQuery(id+"F7.boolean.opBoolean","INTERSECT",EDGE,{"derivedFrom":[makeQuery(id+"F3.opExtrude","SWEPT_FACE",FACE,{"disambiguationData":[OSD([sQuery(id+"F2.wireOp",EDGE,"jYso9TrC-VrG6-bpdd-wlHX-91mLgS95FXrc.left")])]}),makeQuery(id+"F7.opExtrude","SWEPT_FACE",FACE,{"disambiguationData":[OSD([sQuery(id+"F6.wireOp",EDGE,"E8")])]})]});
            var Q23;
            Q23=makeQuery(id+"F1.opExtrude","SWEPT_FACE",FACE,{"disambiguationData":[OSD([sQuery(id+"F0.wireOp",EDGE,"E3.MirrorCS")])]});
            var Q24;
            {var subQ0=sQuery(id+"F2.wireOp",EDGE,"kwgpZEqd-2C8t-yznH-LOjq-w4z4yBxY72GK.right");Q24=makeQuery(id+"F7.boolean.opBoolean","SPLIT",EDGE,{"disambiguationData":[TD([makeQuery(id+"F7.opExtrude","SWEPT_FACE",FACE,{"disambiguationData":[OSD([sQuery(id+"F6.wireOp",EDGE,"E10.1.0.0")])]})])],"derivedFrom":makeQuery(id+"F3.opExtrude","CAP_EDGE",EDGE,{"disambiguationData":[OSD([subQ0])],"isStart":true})});}
            var Q25;
            {var subQ0=sQuery(id+"F2.wireOp",EDGE,"kwgpZEqd-2C8t-yznH-LOjq-w4z4yBxY72GK.right");Q25=makeQuery(id+"F7.boolean.opBoolean","SPLIT",EDGE,{"disambiguationData":[TD([makeQuery(id+"F7.opExtrude","SWEPT_FACE",FACE,{"disambiguationData":[OSD([sQuery(id+"F6.wireOp",EDGE,"E9")])]})])],"derivedFrom":makeQuery(id+"F3.opExtrude","CAP_EDGE",EDGE,{"disambiguationData":[OSD([subQ0])],"isStart":true})});}
            var Q26;
            {var subQ0=sQuery(id+"F2.wireOp",EDGE,"kwgpZEqd-2C8t-yznH-LOjq-w4z4yBxY72GK.right");var subQ1=sQuery(id+"F2.wireOp",EDGE,"kwgpZEqd-2C8t-yznH-LOjq-w4z4yBxY72GK.top");Q26=makeQuery(id+"F7.boolean.opBoolean","SPLIT",EDGE,{"disambiguationData":[TD([makeQuery(id+"F3.opExtrude","SWEPT_FACE",FACE,{"disambiguationData":[OSD([subQ1])]})])],"derivedFrom":makeQuery(id+"F3.opExtrude","CAP_EDGE",EDGE,{"disambiguationData":[OSD([subQ0])],"isStart":true})});}
            var Q27;
            {var subQ0=sQuery(id+"F2.wireOp",EDGE,"kwgpZEqd-2C8t-yznH-LOjq-w4z4yBxY72GK.right");Q27=makeQuery(id+"F7.boolean.opBoolean","SPLIT",EDGE,{"disambiguationData":[TD([makeQuery(id+"F7.opExtrude","SWEPT_FACE",FACE,{"disambiguationData":[OSD([sQuery(id+"F6.wireOp",EDGE,"E10.2.0.0")])]})])],"derivedFrom":makeQuery(id+"F3.opExtrude","CAP_EDGE",EDGE,{"disambiguationData":[OSD([subQ0])],"isStart":true})});}
            var Q28;
            {var subQ0=sQuery(id+"F2.wireOp",EDGE,"kwgpZEqd-2C8t-yznH-LOjq-w4z4yBxY72GK.right");Q28=makeQuery(id+"F7.boolean.opBoolean","SPLIT",EDGE,{"disambiguationData":[TD([makeQuery(id+"F7.opExtrude","SWEPT_FACE",FACE,{"disambiguationData":[OSD([sQuery(id+"F6.wireOp",EDGE,"E10.3.0.0")])]})])],"derivedFrom":makeQuery(id+"F3.opExtrude","CAP_EDGE",EDGE,{"disambiguationData":[OSD([subQ0])],"isStart":true})});}
            var Q29;
            {var subQ0=sQuery(id+"F2.wireOp",EDGE,"kwgpZEqd-2C8t-yznH-LOjq-w4z4yBxY72GK.bottom");var subQ1=sQuery(id+"F2.wireOp",EDGE,"kwgpZEqd-2C8t-yznH-LOjq-w4z4yBxY72GK.right");Q29=makeQuery(id+"F7.boolean.opBoolean","SPLIT",EDGE,{"disambiguationData":[TD([makeQuery(id+"F3.opExtrude","SWEPT_FACE",FACE,{"disambiguationData":[OSD([subQ0])]})])],"derivedFrom":makeQuery(id+"F3.opExtrude","CAP_EDGE",EDGE,{"disambiguationData":[OSD([subQ1])],"isStart":true})});}
            var Q30;
            Q30=makeQuery(id+"F7.boolean.opBoolean","INTERSECT",EDGE,{"derivedFrom":[makeQuery(id+"F3.opExtrude","SWEPT_FACE",FACE,{"disambiguationData":[OSD([sQuery(id+"F2.wireOp",EDGE,"kwgpZEqd-2C8t-yznH-LOjq-w4z4yBxY72GK.right")])]}),makeQuery(id+"F7.opExtrude","SWEPT_FACE",FACE,{"disambiguationData":[OSD([sQuery(id+"F6.wireOp",EDGE,"E10.4.0.1")])]})]});
            var Q31;
            Q31=makeQuery(id+"F7.boolean.opBoolean","INTERSECT",EDGE,{"derivedFrom":[makeQuery(id+"F3.opExtrude","SWEPT_FACE",FACE,{"disambiguationData":[OSD([sQuery(id+"F2.wireOp",EDGE,"kwgpZEqd-2C8t-yznH-LOjq-w4z4yBxY72GK.right")])]}),makeQuery(id+"F7.opExtrude","SWEPT_FACE",FACE,{"disambiguationData":[OSD([sQuery(id+"F6.wireOp",EDGE,"E10.3.0.1")])]})]});
            var Q32;
            Q32=makeQuery(id+"F7.boolean.opBoolean","INTERSECT",EDGE,{"derivedFrom":[makeQuery(id+"F3.opExtrude","SWEPT_FACE",FACE,{"disambiguationData":[OSD([sQuery(id+"F2.wireOp",EDGE,"kwgpZEqd-2C8t-yznH-LOjq-w4z4yBxY72GK.right")])]}),makeQuery(id+"F7.opExtrude","SWEPT_FACE",FACE,{"disambiguationData":[OSD([sQuery(id+"F6.wireOp",EDGE,"E10.2.0.1")])]})]});
            var Q33;
            Q33=makeQuery(id+"F7.boolean.opBoolean","INTERSECT",EDGE,{"derivedFrom":[makeQuery(id+"F3.opExtrude","SWEPT_FACE",FACE,{"disambiguationData":[OSD([sQuery(id+"F2.wireOp",EDGE,"kwgpZEqd-2C8t-yznH-LOjq-w4z4yBxY72GK.right")])]}),makeQuery(id+"F7.opExtrude","SWEPT_FACE",FACE,{"disambiguationData":[OSD([sQuery(id+"F6.wireOp",EDGE,"E10.1.0.1")])]})]});
            var Q34;
            Q34=makeQuery(id+"F7.boolean.opBoolean","INTERSECT",EDGE,{"derivedFrom":[makeQuery(id+"F3.opExtrude","SWEPT_FACE",FACE,{"disambiguationData":[OSD([sQuery(id+"F2.wireOp",EDGE,"kwgpZEqd-2C8t-yznH-LOjq-w4z4yBxY72GK.right")])]}),makeQuery(id+"F7.opExtrude","SWEPT_FACE",FACE,{"disambiguationData":[OSD([sQuery(id+"F6.wireOp",EDGE,"E8")])]})]});
            var Q35;
            {var subQ0=sQuery(id+"F2.wireOp",EDGE,"jYso9TrC-VrG6-bpdd-wlHX-91mLgS95FXrc.right");var subQ1=sQuery(id+"F2.wireOp",EDGE,"jYso9TrC-VrG6-bpdd-wlHX-91mLgS95FXrc.top");Q35=makeQuery(id+"F7.boolean.opBoolean","SPLIT",EDGE,{"disambiguationData":[TD([makeQuery(id+"F3.opExtrude","SWEPT_FACE",FACE,{"disambiguationData":[OSD([subQ1])]})])],"derivedFrom":makeQuery(id+"F3.opExtrude","CAP_EDGE",EDGE,{"disambiguationData":[OSD([subQ0])],"isStart":false})});}
            var Q36;
            Q36=makeQuery(id+"Fou14xSP3GQJlB0_5.boolean.opBoolean","INTERSECT",EDGE,{"derivedFrom":[makeQuery(id+"F7.boolean.opBoolean","COPY",FACE,{"disambiguationData":[TD([makeQuery(id+"F3.opExtrude","SWEPT_FACE",FACE,{"disambiguationData":[OSD([sQuery(id+"F2.wireOp",EDGE,"jYso9TrC-VrG6-bpdd-wlHX-91mLgS95FXrc.left")])]})])],"derivedFrom":makeQuery(id+"F7.opExtrude","SWEPT_FACE",FACE,{"disambiguationData":[OSD([sQuery(id+"F6.wireOp",EDGE,"E28.MirrorCS")])]})}),makeQuery(id+"Fou14xSP3GQJlB0_5.opExtrude","SWEPT_FACE",FACE,{"disambiguationData":[OSD([sQuery(id+"Ffmn4ZGQaAwYWcj_5.wireOp",EDGE,"a3c56a51-e62f-46ba-aa57-5dfe259011c518.MirrorCS")])]})]});
            var Q37;
            {var subQ0=sQuery(id+"F2.wireOp",EDGE,"jYso9TrC-VrG6-bpdd-wlHX-91mLgS95FXrc.right");Q37=makeQuery(id+"F7.boolean.opBoolean","SPLIT",EDGE,{"disambiguationData":[TD([makeQuery(id+"F7.opExtrude","SWEPT_FACE",FACE,{"disambiguationData":[OSD([sQuery(id+"F6.wireOp",EDGE,"E20.MirrorCS")])]})])],"derivedFrom":makeQuery(id+"F3.opExtrude","CAP_EDGE",EDGE,{"disambiguationData":[OSD([subQ0])],"isStart":false})});}
            var Q38;
            Q38=makeQuery(id+"Fou14xSP3GQJlB0_5.boolean.opBoolean","INTERSECT",EDGE,{"derivedFrom":[makeQuery(id+"F7.boolean.opBoolean","COPY",FACE,{"disambiguationData":[TD([makeQuery(id+"F3.opExtrude","SWEPT_FACE",FACE,{"disambiguationData":[OSD([sQuery(id+"F2.wireOp",EDGE,"jYso9TrC-VrG6-bpdd-wlHX-91mLgS95FXrc.left")])]})])],"derivedFrom":makeQuery(id+"F7.opExtrude","SWEPT_FACE",FACE,{"disambiguationData":[OSD([sQuery(id+"F6.wireOp",EDGE,"E36.MirrorCS")])]})}),makeQuery(id+"Fou14xSP3GQJlB0_5.opExtrude","SWEPT_FACE",FACE,{"disambiguationData":[OSD([sQuery(id+"Ffmn4ZGQaAwYWcj_5.wireOp",EDGE,"a3c56a51-e62f-46ba-aa57-5dfe259011c520.MirrorCS")])]})]});
            var Q39;
            {var subQ0=sQuery(id+"F2.wireOp",EDGE,"jYso9TrC-VrG6-bpdd-wlHX-91mLgS95FXrc.right");Q39=makeQuery(id+"F7.boolean.opBoolean","SPLIT",EDGE,{"disambiguationData":[TD([makeQuery(id+"F7.opExtrude","SWEPT_FACE",FACE,{"disambiguationData":[OSD([sQuery(id+"F6.wireOp",EDGE,"E21.MirrorCS")])]})])],"derivedFrom":makeQuery(id+"F3.opExtrude","CAP_EDGE",EDGE,{"disambiguationData":[OSD([subQ0])],"isStart":false})});}
            var Q40;
            Q40=makeQuery(id+"Fou14xSP3GQJlB0_5.boolean.opBoolean","INTERSECT",EDGE,{"derivedFrom":[makeQuery(id+"F7.boolean.opBoolean","COPY",FACE,{"disambiguationData":[TD([makeQuery(id+"F3.opExtrude","SWEPT_FACE",FACE,{"disambiguationData":[OSD([sQuery(id+"F2.wireOp",EDGE,"jYso9TrC-VrG6-bpdd-wlHX-91mLgS95FXrc.left")])]})])],"derivedFrom":makeQuery(id+"F7.opExtrude","SWEPT_FACE",FACE,{"disambiguationData":[OSD([sQuery(id+"F6.wireOp",EDGE,"E37.MirrorCS")])]})}),makeQuery(id+"Fou14xSP3GQJlB0_5.opExtrude","SWEPT_FACE",FACE,{"disambiguationData":[OSD([sQuery(id+"Ffmn4ZGQaAwYWcj_5.wireOp",EDGE,"a3c56a51-e62f-46ba-aa57-5dfe259011c58.MirrorCS")])]})]});
            var Q41;
            {var subQ0=sQuery(id+"F2.wireOp",EDGE,"jYso9TrC-VrG6-bpdd-wlHX-91mLgS95FXrc.right");Q41=makeQuery(id+"F7.boolean.opBoolean","SPLIT",EDGE,{"disambiguationData":[TD([makeQuery(id+"F7.opExtrude","SWEPT_FACE",FACE,{"disambiguationData":[OSD([sQuery(id+"F6.wireOp",EDGE,"E18.MirrorCS")])]})])],"derivedFrom":makeQuery(id+"F3.opExtrude","CAP_EDGE",EDGE,{"disambiguationData":[OSD([subQ0])],"isStart":false})});}
            var Q42;
            Q42=makeQuery(id+"Fou14xSP3GQJlB0_5.boolean.opBoolean","INTERSECT",EDGE,{"derivedFrom":[makeQuery(id+"F7.boolean.opBoolean","COPY",FACE,{"disambiguationData":[TD([makeQuery(id+"F3.opExtrude","SWEPT_FACE",FACE,{"disambiguationData":[OSD([sQuery(id+"F2.wireOp",EDGE,"jYso9TrC-VrG6-bpdd-wlHX-91mLgS95FXrc.left")])]})])],"derivedFrom":makeQuery(id+"F7.opExtrude","SWEPT_FACE",FACE,{"disambiguationData":[OSD([sQuery(id+"F6.wireOp",EDGE,"E29.MirrorCS")])]})}),makeQuery(id+"Fou14xSP3GQJlB0_5.opExtrude","SWEPT_FACE",FACE,{"disambiguationData":[OSD([sQuery(id+"Ffmn4ZGQaAwYWcj_5.wireOp",EDGE,"a3c56a51-e62f-46ba-aa57-5dfe259011c59.MirrorCS")])]})]});
            var Q43;
            {var subQ0=sQuery(id+"F2.wireOp",EDGE,"jYso9TrC-VrG6-bpdd-wlHX-91mLgS95FXrc.right");Q43=makeQuery(id+"F7.boolean.opBoolean","SPLIT",EDGE,{"disambiguationData":[TD([makeQuery(id+"F7.opExtrude","SWEPT_FACE",FACE,{"disambiguationData":[OSD([sQuery(id+"F6.wireOp",EDGE,"E25.MirrorCS")])]})])],"derivedFrom":makeQuery(id+"F3.opExtrude","CAP_EDGE",EDGE,{"disambiguationData":[OSD([subQ0])],"isStart":false})});}
            var Q44;
            Q44=makeQuery(id+"Fou14xSP3GQJlB0_5.boolean.opBoolean","INTERSECT",EDGE,{"derivedFrom":[makeQuery(id+"F7.boolean.opBoolean","COPY",FACE,{"disambiguationData":[TD([makeQuery(id+"F3.opExtrude","SWEPT_FACE",FACE,{"disambiguationData":[OSD([sQuery(id+"F2.wireOp",EDGE,"jYso9TrC-VrG6-bpdd-wlHX-91mLgS95FXrc.left")])]})])],"derivedFrom":makeQuery(id+"F7.opExtrude","SWEPT_FACE",FACE,{"disambiguationData":[OSD([sQuery(id+"F6.wireOp",EDGE,"E33.MirrorCS")])]})}),makeQuery(id+"Fou14xSP3GQJlB0_5.opExtrude","SWEPT_FACE",FACE,{"disambiguationData":[OSD([sQuery(id+"Ffmn4ZGQaAwYWcj_5.wireOp",EDGE,"a3c56a51-e62f-46ba-aa57-5dfe259011c510.MirrorCS")])]})]});
            var Q45;
            {var subQ0=sQuery(id+"F2.wireOp",EDGE,"jYso9TrC-VrG6-bpdd-wlHX-91mLgS95FXrc.bottom");var subQ1=sQuery(id+"F2.wireOp",EDGE,"jYso9TrC-VrG6-bpdd-wlHX-91mLgS95FXrc.right");Q45=makeQuery(id+"F7.boolean.opBoolean","SPLIT",EDGE,{"disambiguationData":[TD([makeQuery(id+"F3.opExtrude","SWEPT_FACE",FACE,{"disambiguationData":[OSD([subQ0])]})])],"derivedFrom":makeQuery(id+"F3.opExtrude","CAP_EDGE",EDGE,{"disambiguationData":[OSD([subQ1])],"isStart":false})});}
            var Q46;
            {var subQ0=sQuery(id+"F2.wireOp",EDGE,"jYso9TrC-VrG6-bpdd-wlHX-91mLgS95FXrc.left");var subQ1=sQuery(id+"F2.wireOp",EDGE,"jYso9TrC-VrG6-bpdd-wlHX-91mLgS95FXrc.top");Q46=makeQuery(id+"F7.boolean.opBoolean","SPLIT",EDGE,{"disambiguationData":[TD([makeQuery(id+"F3.opExtrude","SWEPT_FACE",FACE,{"disambiguationData":[OSD([subQ1])]})])],"derivedFrom":makeQuery(id+"F3.opExtrude","CAP_EDGE",EDGE,{"disambiguationData":[OSD([subQ0])],"isStart":false})});}
            var Q47;
            Q47=makeQuery(id+"F7.boolean.opBoolean","INTERSECT",EDGE,{"derivedFrom":[makeQuery(id+"F3.opExtrude","SWEPT_FACE",FACE,{"disambiguationData":[OSD([sQuery(id+"F2.wireOp",EDGE,"jYso9TrC-VrG6-bpdd-wlHX-91mLgS95FXrc.left")])]}),makeQuery(id+"F7.opExtrude","SWEPT_FACE",FACE,{"disambiguationData":[OSD([sQuery(id+"F6.wireOp",EDGE,"E28.MirrorCS")])]})]});
            var Q48;
            {var subQ0=sQuery(id+"F2.wireOp",EDGE,"jYso9TrC-VrG6-bpdd-wlHX-91mLgS95FXrc.left");Q48=makeQuery(id+"F7.boolean.opBoolean","SPLIT",EDGE,{"disambiguationData":[TD([makeQuery(id+"F7.opExtrude","SWEPT_FACE",FACE,{"disambiguationData":[OSD([sQuery(id+"F6.wireOp",EDGE,"E20.MirrorCS")])]})])],"derivedFrom":makeQuery(id+"F3.opExtrude","CAP_EDGE",EDGE,{"disambiguationData":[OSD([subQ0])],"isStart":false})});}
            var Q49;
            Q49=makeQuery(id+"F7.boolean.opBoolean","INTERSECT",EDGE,{"derivedFrom":[makeQuery(id+"F3.opExtrude","SWEPT_FACE",FACE,{"disambiguationData":[OSD([sQuery(id+"F2.wireOp",EDGE,"jYso9TrC-VrG6-bpdd-wlHX-91mLgS95FXrc.left")])]}),makeQuery(id+"F7.opExtrude","SWEPT_FACE",FACE,{"disambiguationData":[OSD([sQuery(id+"F6.wireOp",EDGE,"E36.MirrorCS")])]})]});
            var Q50;
            {var subQ0=sQuery(id+"F2.wireOp",EDGE,"jYso9TrC-VrG6-bpdd-wlHX-91mLgS95FXrc.left");Q50=makeQuery(id+"F7.boolean.opBoolean","SPLIT",EDGE,{"disambiguationData":[TD([makeQuery(id+"F7.opExtrude","SWEPT_FACE",FACE,{"disambiguationData":[OSD([sQuery(id+"F6.wireOp",EDGE,"E21.MirrorCS")])]})])],"derivedFrom":makeQuery(id+"F3.opExtrude","CAP_EDGE",EDGE,{"disambiguationData":[OSD([subQ0])],"isStart":false})});}
            var Q51;
            Q51=makeQuery(id+"F7.boolean.opBoolean","INTERSECT",EDGE,{"derivedFrom":[makeQuery(id+"F3.opExtrude","SWEPT_FACE",FACE,{"disambiguationData":[OSD([sQuery(id+"F2.wireOp",EDGE,"jYso9TrC-VrG6-bpdd-wlHX-91mLgS95FXrc.left")])]}),makeQuery(id+"F7.opExtrude","SWEPT_FACE",FACE,{"disambiguationData":[OSD([sQuery(id+"F6.wireOp",EDGE,"E37.MirrorCS")])]})]});
            var Q52;
            {var subQ0=sQuery(id+"F2.wireOp",EDGE,"jYso9TrC-VrG6-bpdd-wlHX-91mLgS95FXrc.left");Q52=makeQuery(id+"F7.boolean.opBoolean","SPLIT",EDGE,{"disambiguationData":[TD([makeQuery(id+"F7.opExtrude","SWEPT_FACE",FACE,{"disambiguationData":[OSD([sQuery(id+"F6.wireOp",EDGE,"E18.MirrorCS")])]})])],"derivedFrom":makeQuery(id+"F3.opExtrude","CAP_EDGE",EDGE,{"disambiguationData":[OSD([subQ0])],"isStart":false})});}
            var Q53;
            Q53=makeQuery(id+"F7.boolean.opBoolean","INTERSECT",EDGE,{"derivedFrom":[makeQuery(id+"F3.opExtrude","SWEPT_FACE",FACE,{"disambiguationData":[OSD([sQuery(id+"F2.wireOp",EDGE,"jYso9TrC-VrG6-bpdd-wlHX-91mLgS95FXrc.left")])]}),makeQuery(id+"F7.opExtrude","SWEPT_FACE",FACE,{"disambiguationData":[OSD([sQuery(id+"F6.wireOp",EDGE,"E29.MirrorCS")])]})]});
            var Q54;
            {var subQ0=sQuery(id+"F2.wireOp",EDGE,"jYso9TrC-VrG6-bpdd-wlHX-91mLgS95FXrc.left");Q54=makeQuery(id+"F7.boolean.opBoolean","SPLIT",EDGE,{"disambiguationData":[TD([makeQuery(id+"F7.opExtrude","SWEPT_FACE",FACE,{"disambiguationData":[OSD([sQuery(id+"F6.wireOp",EDGE,"E25.MirrorCS")])]})])],"derivedFrom":makeQuery(id+"F3.opExtrude","CAP_EDGE",EDGE,{"disambiguationData":[OSD([subQ0])],"isStart":false})});}
            var Q55;
            Q55=makeQuery(id+"F7.boolean.opBoolean","INTERSECT",EDGE,{"derivedFrom":[makeQuery(id+"F3.opExtrude","SWEPT_FACE",FACE,{"disambiguationData":[OSD([sQuery(id+"F2.wireOp",EDGE,"jYso9TrC-VrG6-bpdd-wlHX-91mLgS95FXrc.left")])]}),makeQuery(id+"F7.opExtrude","SWEPT_FACE",FACE,{"disambiguationData":[OSD([sQuery(id+"F6.wireOp",EDGE,"E33.MirrorCS")])]})]});
            var Q56;
            {var subQ0=sQuery(id+"F2.wireOp",EDGE,"jYso9TrC-VrG6-bpdd-wlHX-91mLgS95FXrc.bottom");var subQ1=sQuery(id+"F2.wireOp",EDGE,"jYso9TrC-VrG6-bpdd-wlHX-91mLgS95FXrc.left");Q56=makeQuery(id+"F7.boolean.opBoolean","SPLIT",EDGE,{"disambiguationData":[TD([makeQuery(id+"F3.opExtrude","SWEPT_FACE",FACE,{"disambiguationData":[OSD([subQ0])]})])],"derivedFrom":makeQuery(id+"F3.opExtrude","CAP_EDGE",EDGE,{"disambiguationData":[OSD([subQ1])],"isStart":false})});}
            var Q57;
            {var subQ0=sQuery(id+"F2.wireOp",EDGE,"kwgpZEqd-2C8t-yznH-LOjq-w4z4yBxY72GK.bottom");var subQ1=sQuery(id+"F2.wireOp",EDGE,"kwgpZEqd-2C8t-yznH-LOjq-w4z4yBxY72GK.right");Q57=makeQuery(id+"F7.boolean.opBoolean","SPLIT",EDGE,{"disambiguationData":[TD([makeQuery(id+"F3.opExtrude","SWEPT_FACE",FACE,{"disambiguationData":[OSD([subQ0])]})])],"derivedFrom":makeQuery(id+"F3.opExtrude","CAP_EDGE",EDGE,{"disambiguationData":[OSD([subQ1])],"isStart":false})});}
            var Q58;
            Q58=makeQuery(id+"F7.boolean.opBoolean","INTERSECT",EDGE,{"derivedFrom":[makeQuery(id+"F3.opExtrude","SWEPT_FACE",FACE,{"disambiguationData":[OSD([sQuery(id+"F2.wireOp",EDGE,"kwgpZEqd-2C8t-yznH-LOjq-w4z4yBxY72GK.right")])]}),makeQuery(id+"F7.opExtrude","SWEPT_FACE",FACE,{"disambiguationData":[OSD([sQuery(id+"F6.wireOp",EDGE,"E33.MirrorCS")])]})]});
            var Q59;
            {var subQ0=sQuery(id+"F2.wireOp",EDGE,"kwgpZEqd-2C8t-yznH-LOjq-w4z4yBxY72GK.right");Q59=makeQuery(id+"F7.boolean.opBoolean","SPLIT",EDGE,{"disambiguationData":[TD([makeQuery(id+"F7.opExtrude","SWEPT_FACE",FACE,{"disambiguationData":[OSD([sQuery(id+"F6.wireOp",EDGE,"E25.MirrorCS")])]})])],"derivedFrom":makeQuery(id+"F3.opExtrude","CAP_EDGE",EDGE,{"disambiguationData":[OSD([subQ0])],"isStart":false})});}
            var Q60;
            Q60=makeQuery(id+"F7.boolean.opBoolean","INTERSECT",EDGE,{"derivedFrom":[makeQuery(id+"F3.opExtrude","SWEPT_FACE",FACE,{"disambiguationData":[OSD([sQuery(id+"F2.wireOp",EDGE,"kwgpZEqd-2C8t-yznH-LOjq-w4z4yBxY72GK.right")])]}),makeQuery(id+"F7.opExtrude","SWEPT_FACE",FACE,{"disambiguationData":[OSD([sQuery(id+"F6.wireOp",EDGE,"E29.MirrorCS")])]})]});
            var Q61;
            {var subQ0=sQuery(id+"F2.wireOp",EDGE,"kwgpZEqd-2C8t-yznH-LOjq-w4z4yBxY72GK.right");Q61=makeQuery(id+"F7.boolean.opBoolean","SPLIT",EDGE,{"disambiguationData":[TD([makeQuery(id+"F7.opExtrude","SWEPT_FACE",FACE,{"disambiguationData":[OSD([sQuery(id+"F6.wireOp",EDGE,"E18.MirrorCS")])]})])],"derivedFrom":makeQuery(id+"F3.opExtrude","CAP_EDGE",EDGE,{"disambiguationData":[OSD([subQ0])],"isStart":false})});}
            var Q62;
            Q62=makeQuery(id+"F7.boolean.opBoolean","INTERSECT",EDGE,{"derivedFrom":[makeQuery(id+"F3.opExtrude","SWEPT_FACE",FACE,{"disambiguationData":[OSD([sQuery(id+"F2.wireOp",EDGE,"kwgpZEqd-2C8t-yznH-LOjq-w4z4yBxY72GK.right")])]}),makeQuery(id+"F7.opExtrude","SWEPT_FACE",FACE,{"disambiguationData":[OSD([sQuery(id+"F6.wireOp",EDGE,"E37.MirrorCS")])]})]});
            var Q63;
            {var subQ0=sQuery(id+"F2.wireOp",EDGE,"kwgpZEqd-2C8t-yznH-LOjq-w4z4yBxY72GK.right");Q63=makeQuery(id+"F7.boolean.opBoolean","SPLIT",EDGE,{"disambiguationData":[TD([makeQuery(id+"F7.opExtrude","SWEPT_FACE",FACE,{"disambiguationData":[OSD([sQuery(id+"F6.wireOp",EDGE,"E21.MirrorCS")])]})])],"derivedFrom":makeQuery(id+"F3.opExtrude","CAP_EDGE",EDGE,{"disambiguationData":[OSD([subQ0])],"isStart":false})});}
            var Q64;
            Q64=makeQuery(id+"F7.boolean.opBoolean","INTERSECT",EDGE,{"derivedFrom":[makeQuery(id+"F3.opExtrude","SWEPT_FACE",FACE,{"disambiguationData":[OSD([sQuery(id+"F2.wireOp",EDGE,"kwgpZEqd-2C8t-yznH-LOjq-w4z4yBxY72GK.right")])]}),makeQuery(id+"F7.opExtrude","SWEPT_FACE",FACE,{"disambiguationData":[OSD([sQuery(id+"F6.wireOp",EDGE,"E36.MirrorCS")])]})]});
            var Q65;
            {var subQ0=sQuery(id+"F2.wireOp",EDGE,"kwgpZEqd-2C8t-yznH-LOjq-w4z4yBxY72GK.right");Q65=makeQuery(id+"F7.boolean.opBoolean","SPLIT",EDGE,{"disambiguationData":[TD([makeQuery(id+"F7.opExtrude","SWEPT_FACE",FACE,{"disambiguationData":[OSD([sQuery(id+"F6.wireOp",EDGE,"E20.MirrorCS")])]})])],"derivedFrom":makeQuery(id+"F3.opExtrude","CAP_EDGE",EDGE,{"disambiguationData":[OSD([subQ0])],"isStart":false})});}
            var Q66;
            Q66=makeQuery(id+"F7.boolean.opBoolean","INTERSECT",EDGE,{"derivedFrom":[makeQuery(id+"F3.opExtrude","SWEPT_FACE",FACE,{"disambiguationData":[OSD([sQuery(id+"F2.wireOp",EDGE,"kwgpZEqd-2C8t-yznH-LOjq-w4z4yBxY72GK.right")])]}),makeQuery(id+"F7.opExtrude","SWEPT_FACE",FACE,{"disambiguationData":[OSD([sQuery(id+"F6.wireOp",EDGE,"E28.MirrorCS")])]})]});
            var Q67;
            {var subQ0=sQuery(id+"F2.wireOp",EDGE,"kwgpZEqd-2C8t-yznH-LOjq-w4z4yBxY72GK.right");var subQ1=sQuery(id+"F2.wireOp",EDGE,"kwgpZEqd-2C8t-yznH-LOjq-w4z4yBxY72GK.top");Q67=makeQuery(id+"F7.boolean.opBoolean","SPLIT",EDGE,{"disambiguationData":[TD([makeQuery(id+"F3.opExtrude","SWEPT_FACE",FACE,{"disambiguationData":[OSD([subQ1])]})])],"derivedFrom":makeQuery(id+"F3.opExtrude","CAP_EDGE",EDGE,{"disambiguationData":[OSD([subQ0])],"isStart":false})});}
            var Q68;
            {var subQ0=sQuery(id+"F2.wireOp",EDGE,"kwgpZEqd-2C8t-yznH-LOjq-w4z4yBxY72GK.left");var subQ1=sQuery(id+"F2.wireOp",EDGE,"kwgpZEqd-2C8t-yznH-LOjq-w4z4yBxY72GK.top");Q68=makeQuery(id+"F7.boolean.opBoolean","SPLIT",EDGE,{"disambiguationData":[TD([makeQuery(id+"F3.opExtrude","SWEPT_FACE",FACE,{"disambiguationData":[OSD([subQ1])]})])],"derivedFrom":makeQuery(id+"F3.opExtrude","CAP_EDGE",EDGE,{"disambiguationData":[OSD([subQ0])],"isStart":false})});}
            var Q69;
            {var subQ0=sQuery(id+"F2.wireOp",EDGE,"kwgpZEqd-2C8t-yznH-LOjq-w4z4yBxY72GK.left");Q69=makeQuery(id+"F7.boolean.opBoolean","SPLIT",EDGE,{"disambiguationData":[TD([makeQuery(id+"F7.opExtrude","SWEPT_FACE",FACE,{"disambiguationData":[OSD([sQuery(id+"F6.wireOp",EDGE,"E20.MirrorCS")])]})])],"derivedFrom":makeQuery(id+"F3.opExtrude","CAP_EDGE",EDGE,{"disambiguationData":[OSD([subQ0])],"isStart":false})});}
            var Q70;
            Q70=makeQuery(id+"F7.boolean.opBoolean","INTERSECT",EDGE,{"derivedFrom":[makeQuery(id+"F3.opExtrude","SWEPT_FACE",FACE,{"disambiguationData":[OSD([sQuery(id+"F2.wireOp",EDGE,"kwgpZEqd-2C8t-yznH-LOjq-w4z4yBxY72GK.left")])]}),makeQuery(id+"F7.opExtrude","SWEPT_FACE",FACE,{"disambiguationData":[OSD([sQuery(id+"F6.wireOp",EDGE,"E36.MirrorCS")])]})]});
            var Q71;
            {var subQ0=sQuery(id+"F2.wireOp",EDGE,"kwgpZEqd-2C8t-yznH-LOjq-w4z4yBxY72GK.left");Q71=makeQuery(id+"F7.boolean.opBoolean","SPLIT",EDGE,{"disambiguationData":[TD([makeQuery(id+"F7.opExtrude","SWEPT_FACE",FACE,{"disambiguationData":[OSD([sQuery(id+"F6.wireOp",EDGE,"E21.MirrorCS")])]})])],"derivedFrom":makeQuery(id+"F3.opExtrude","CAP_EDGE",EDGE,{"disambiguationData":[OSD([subQ0])],"isStart":false})});}
            var Q72;
            Q72=makeQuery(id+"F7.boolean.opBoolean","INTERSECT",EDGE,{"derivedFrom":[makeQuery(id+"F3.opExtrude","SWEPT_FACE",FACE,{"disambiguationData":[OSD([sQuery(id+"F2.wireOp",EDGE,"kwgpZEqd-2C8t-yznH-LOjq-w4z4yBxY72GK.left")])]}),makeQuery(id+"F7.opExtrude","SWEPT_FACE",FACE,{"disambiguationData":[OSD([sQuery(id+"F6.wireOp",EDGE,"E37.MirrorCS")])]})]});
            var Q73;
            {var subQ0=sQuery(id+"F2.wireOp",EDGE,"kwgpZEqd-2C8t-yznH-LOjq-w4z4yBxY72GK.left");Q73=makeQuery(id+"F7.boolean.opBoolean","SPLIT",EDGE,{"disambiguationData":[TD([makeQuery(id+"F7.opExtrude","SWEPT_FACE",FACE,{"disambiguationData":[OSD([sQuery(id+"F6.wireOp",EDGE,"E18.MirrorCS")])]})])],"derivedFrom":makeQuery(id+"F3.opExtrude","CAP_EDGE",EDGE,{"disambiguationData":[OSD([subQ0])],"isStart":false})});}
            var Q74;
            Q74=makeQuery(id+"F7.boolean.opBoolean","INTERSECT",EDGE,{"derivedFrom":[makeQuery(id+"F3.opExtrude","SWEPT_FACE",FACE,{"disambiguationData":[OSD([sQuery(id+"F2.wireOp",EDGE,"kwgpZEqd-2C8t-yznH-LOjq-w4z4yBxY72GK.left")])]}),makeQuery(id+"F7.opExtrude","SWEPT_FACE",FACE,{"disambiguationData":[OSD([sQuery(id+"F6.wireOp",EDGE,"E29.MirrorCS")])]})]});
            var Q75;
            {var subQ0=sQuery(id+"F2.wireOp",EDGE,"kwgpZEqd-2C8t-yznH-LOjq-w4z4yBxY72GK.left");Q75=makeQuery(id+"F7.boolean.opBoolean","SPLIT",EDGE,{"disambiguationData":[TD([makeQuery(id+"F7.opExtrude","SWEPT_FACE",FACE,{"disambiguationData":[OSD([sQuery(id+"F6.wireOp",EDGE,"E25.MirrorCS")])]})])],"derivedFrom":makeQuery(id+"F3.opExtrude","CAP_EDGE",EDGE,{"disambiguationData":[OSD([subQ0])],"isStart":false})});}
            var Q76;
            Q76=makeQuery(id+"F7.boolean.opBoolean","INTERSECT",EDGE,{"derivedFrom":[makeQuery(id+"F3.opExtrude","SWEPT_FACE",FACE,{"disambiguationData":[OSD([sQuery(id+"F2.wireOp",EDGE,"kwgpZEqd-2C8t-yznH-LOjq-w4z4yBxY72GK.left")])]}),makeQuery(id+"F7.opExtrude","SWEPT_FACE",FACE,{"disambiguationData":[OSD([sQuery(id+"F6.wireOp",EDGE,"E33.MirrorCS")])]})]});
            var Q77;
            {var subQ0=sQuery(id+"F2.wireOp",EDGE,"kwgpZEqd-2C8t-yznH-LOjq-w4z4yBxY72GK.bottom");var subQ1=sQuery(id+"F2.wireOp",EDGE,"kwgpZEqd-2C8t-yznH-LOjq-w4z4yBxY72GK.left");Q77=makeQuery(id+"F7.boolean.opBoolean","SPLIT",EDGE,{"disambiguationData":[TD([makeQuery(id+"F3.opExtrude","SWEPT_FACE",FACE,{"disambiguationData":[OSD([subQ0])]})])],"derivedFrom":makeQuery(id+"F3.opExtrude","CAP_EDGE",EDGE,{"disambiguationData":[OSD([subQ1])],"isStart":false})});}
            var Q78;
            Q78=makeQuery(id+"F7.boolean.opBoolean","INTERSECT",EDGE,{"derivedFrom":[makeQuery(id+"F3.opExtrude","SWEPT_FACE",FACE,{"disambiguationData":[OSD([sQuery(id+"F2.wireOp",EDGE,"kwgpZEqd-2C8t-yznH-LOjq-w4z4yBxY72GK.left")])]}),makeQuery(id+"F7.opExtrude","SWEPT_FACE",FACE,{"disambiguationData":[OSD([sQuery(id+"F6.wireOp",EDGE,"E28.MirrorCS")])]})]});
            var Q79;
            {var subQ0=sQuery(id+"F2.wireOp",EDGE,"0J23cXKG-jTpq-C0wa-xp2X-HWyvlrIdDXZe.left");var subQ1=sQuery(id+"F2.wireOp",EDGE,"0J23cXKG-jTpq-C0wa-xp2X-HWyvlrIdDXZe.top");Q79=makeQuery(id+"F7.boolean.opBoolean","SPLIT",EDGE,{"disambiguationData":[TD([makeQuery(id+"F3.opExtrude","SWEPT_FACE",FACE,{"disambiguationData":[OSD([subQ1])]})])],"derivedFrom":makeQuery(id+"F3.opExtrude","CAP_EDGE",EDGE,{"disambiguationData":[OSD([subQ0])],"isStart":false})});}
            var Q80;
            Q80=makeQuery(id+"F7.boolean.opBoolean","INTERSECT",EDGE,{"derivedFrom":[makeQuery(id+"F3.opExtrude","SWEPT_FACE",FACE,{"disambiguationData":[OSD([sQuery(id+"F2.wireOp",EDGE,"0J23cXKG-jTpq-C0wa-xp2X-HWyvlrIdDXZe.left")])]}),makeQuery(id+"F7.opExtrude","SWEPT_FACE",FACE,{"disambiguationData":[OSD([sQuery(id+"F6.wireOp",EDGE,"E28.MirrorCS")])]})]});
            var Q81;
            {var subQ0=sQuery(id+"F2.wireOp",EDGE,"0J23cXKG-jTpq-C0wa-xp2X-HWyvlrIdDXZe.left");Q81=makeQuery(id+"F7.boolean.opBoolean","SPLIT",EDGE,{"disambiguationData":[TD([makeQuery(id+"F7.opExtrude","SWEPT_FACE",FACE,{"disambiguationData":[OSD([sQuery(id+"F6.wireOp",EDGE,"E20.MirrorCS")])]})])],"derivedFrom":makeQuery(id+"F3.opExtrude","CAP_EDGE",EDGE,{"disambiguationData":[OSD([subQ0])],"isStart":false})});}
            var Q82;
            Q82=makeQuery(id+"F7.boolean.opBoolean","INTERSECT",EDGE,{"derivedFrom":[makeQuery(id+"F3.opExtrude","SWEPT_FACE",FACE,{"disambiguationData":[OSD([sQuery(id+"F2.wireOp",EDGE,"0J23cXKG-jTpq-C0wa-xp2X-HWyvlrIdDXZe.left")])]}),makeQuery(id+"F7.opExtrude","SWEPT_FACE",FACE,{"disambiguationData":[OSD([sQuery(id+"F6.wireOp",EDGE,"E36.MirrorCS")])]})]});
            var Q83;
            {var subQ0=sQuery(id+"F2.wireOp",EDGE,"0J23cXKG-jTpq-C0wa-xp2X-HWyvlrIdDXZe.left");Q83=makeQuery(id+"F7.boolean.opBoolean","SPLIT",EDGE,{"disambiguationData":[TD([makeQuery(id+"F7.opExtrude","SWEPT_FACE",FACE,{"disambiguationData":[OSD([sQuery(id+"F6.wireOp",EDGE,"E21.MirrorCS")])]})])],"derivedFrom":makeQuery(id+"F3.opExtrude","CAP_EDGE",EDGE,{"disambiguationData":[OSD([subQ0])],"isStart":false})});}
            var Q84;
            Q84=makeQuery(id+"F7.boolean.opBoolean","INTERSECT",EDGE,{"derivedFrom":[makeQuery(id+"F3.opExtrude","SWEPT_FACE",FACE,{"disambiguationData":[OSD([sQuery(id+"F2.wireOp",EDGE,"0J23cXKG-jTpq-C0wa-xp2X-HWyvlrIdDXZe.left")])]}),makeQuery(id+"F7.opExtrude","SWEPT_FACE",FACE,{"disambiguationData":[OSD([sQuery(id+"F6.wireOp",EDGE,"E37.MirrorCS")])]})]});
            var Q85;
            {var subQ0=sQuery(id+"F2.wireOp",EDGE,"0J23cXKG-jTpq-C0wa-xp2X-HWyvlrIdDXZe.left");Q85=makeQuery(id+"F7.boolean.opBoolean","SPLIT",EDGE,{"disambiguationData":[TD([makeQuery(id+"F7.opExtrude","SWEPT_FACE",FACE,{"disambiguationData":[OSD([sQuery(id+"F6.wireOp",EDGE,"E18.MirrorCS")])]})])],"derivedFrom":makeQuery(id+"F3.opExtrude","CAP_EDGE",EDGE,{"disambiguationData":[OSD([subQ0])],"isStart":false})});}
            var Q86;
            Q86=makeQuery(id+"F7.boolean.opBoolean","INTERSECT",EDGE,{"derivedFrom":[makeQuery(id+"F3.opExtrude","SWEPT_FACE",FACE,{"disambiguationData":[OSD([sQuery(id+"F2.wireOp",EDGE,"0J23cXKG-jTpq-C0wa-xp2X-HWyvlrIdDXZe.left")])]}),makeQuery(id+"F7.opExtrude","SWEPT_FACE",FACE,{"disambiguationData":[OSD([sQuery(id+"F6.wireOp",EDGE,"E29.MirrorCS")])]})]});
            var Q87;
            {var subQ0=sQuery(id+"F2.wireOp",EDGE,"0J23cXKG-jTpq-C0wa-xp2X-HWyvlrIdDXZe.left");Q87=makeQuery(id+"F7.boolean.opBoolean","SPLIT",EDGE,{"disambiguationData":[TD([makeQuery(id+"F7.opExtrude","SWEPT_FACE",FACE,{"disambiguationData":[OSD([sQuery(id+"F6.wireOp",EDGE,"E25.MirrorCS")])]})])],"derivedFrom":makeQuery(id+"F3.opExtrude","CAP_EDGE",EDGE,{"disambiguationData":[OSD([subQ0])],"isStart":false})});}
            var Q88;
            Q88=makeQuery(id+"F7.boolean.opBoolean","INTERSECT",EDGE,{"derivedFrom":[makeQuery(id+"F3.opExtrude","SWEPT_FACE",FACE,{"disambiguationData":[OSD([sQuery(id+"F2.wireOp",EDGE,"0J23cXKG-jTpq-C0wa-xp2X-HWyvlrIdDXZe.left")])]}),makeQuery(id+"F7.opExtrude","SWEPT_FACE",FACE,{"disambiguationData":[OSD([sQuery(id+"F6.wireOp",EDGE,"E33.MirrorCS")])]})]});
            var Q89;
            {var subQ0=sQuery(id+"F2.wireOp",EDGE,"0J23cXKG-jTpq-C0wa-xp2X-HWyvlrIdDXZe.bottom");var subQ1=sQuery(id+"F2.wireOp",EDGE,"0J23cXKG-jTpq-C0wa-xp2X-HWyvlrIdDXZe.left");Q89=makeQuery(id+"F7.boolean.opBoolean","SPLIT",EDGE,{"disambiguationData":[TD([makeQuery(id+"F3.opExtrude","SWEPT_FACE",FACE,{"disambiguationData":[OSD([subQ0])]})])],"derivedFrom":makeQuery(id+"F3.opExtrude","CAP_EDGE",EDGE,{"disambiguationData":[OSD([subQ1])],"isStart":false})});}
            var Q90;
            {var subQ0=sQuery(id+"F2.wireOp",EDGE,"0J23cXKG-jTpq-C0wa-xp2X-HWyvlrIdDXZe.bottom");var subQ1=sQuery(id+"F2.wireOp",EDGE,"0J23cXKG-jTpq-C0wa-xp2X-HWyvlrIdDXZe.right");Q90=makeQuery(id+"F7.boolean.opBoolean","SPLIT",EDGE,{"disambiguationData":[TD([makeQuery(id+"F3.opExtrude","SWEPT_FACE",FACE,{"disambiguationData":[OSD([subQ0])]})])],"derivedFrom":makeQuery(id+"F3.opExtrude","CAP_EDGE",EDGE,{"disambiguationData":[OSD([subQ1])],"isStart":false})});}
            var Q91;
            Q91=makeQuery(id+"Fou14xSP3GQJlB0_5.boolean.opBoolean","INTERSECT",EDGE,{"derivedFrom":[makeQuery(id+"F7.boolean.opBoolean","COPY",FACE,{"disambiguationData":[TD([makeQuery(id+"F3.opExtrude","SWEPT_FACE",FACE,{"disambiguationData":[OSD([sQuery(id+"F2.wireOp",EDGE,"0J23cXKG-jTpq-C0wa-xp2X-HWyvlrIdDXZe.left")])]})])],"derivedFrom":makeQuery(id+"F7.opExtrude","SWEPT_FACE",FACE,{"disambiguationData":[OSD([sQuery(id+"F6.wireOp",EDGE,"E33.MirrorCS")])]})}),makeQuery(id+"Fou14xSP3GQJlB0_5.opExtrude","SWEPT_FACE",FACE,{"disambiguationData":[OSD([sQuery(id+"Ffmn4ZGQaAwYWcj_5.wireOp",EDGE,"5qgGCEaO-EZzk-biRs-uW5n-FUkAzBEinMKw.left")])]})]});
            var Q92;
            {var subQ0=sQuery(id+"F2.wireOp",EDGE,"0J23cXKG-jTpq-C0wa-xp2X-HWyvlrIdDXZe.right");Q92=makeQuery(id+"F7.boolean.opBoolean","SPLIT",EDGE,{"disambiguationData":[TD([makeQuery(id+"F7.opExtrude","SWEPT_FACE",FACE,{"disambiguationData":[OSD([sQuery(id+"F6.wireOp",EDGE,"E25.MirrorCS")])]})])],"derivedFrom":makeQuery(id+"F3.opExtrude","CAP_EDGE",EDGE,{"disambiguationData":[OSD([subQ0])],"isStart":false})});}
            var Q93;
            Q93=makeQuery(id+"Fou14xSP3GQJlB0_5.boolean.opBoolean","INTERSECT",EDGE,{"derivedFrom":[makeQuery(id+"F7.boolean.opBoolean","COPY",FACE,{"disambiguationData":[TD([makeQuery(id+"F3.opExtrude","SWEPT_FACE",FACE,{"disambiguationData":[OSD([sQuery(id+"F2.wireOp",EDGE,"0J23cXKG-jTpq-C0wa-xp2X-HWyvlrIdDXZe.left")])]})])],"derivedFrom":makeQuery(id+"F7.opExtrude","SWEPT_FACE",FACE,{"disambiguationData":[OSD([sQuery(id+"F6.wireOp",EDGE,"E29.MirrorCS")])]})}),makeQuery(id+"Fou14xSP3GQJlB0_5.opExtrude","SWEPT_FACE",FACE,{"disambiguationData":[OSD([sQuery(id+"Ffmn4ZGQaAwYWcj_5.wireOp",EDGE,"83f02070-e68f-438f-992c-3ac59f97bf76.0.1.3")])]})]});
            var Q94;
            {var subQ0=sQuery(id+"F2.wireOp",EDGE,"0J23cXKG-jTpq-C0wa-xp2X-HWyvlrIdDXZe.right");Q94=makeQuery(id+"F7.boolean.opBoolean","SPLIT",EDGE,{"disambiguationData":[TD([makeQuery(id+"F7.opExtrude","SWEPT_FACE",FACE,{"disambiguationData":[OSD([sQuery(id+"F6.wireOp",EDGE,"E18.MirrorCS")])]})])],"derivedFrom":makeQuery(id+"F3.opExtrude","CAP_EDGE",EDGE,{"disambiguationData":[OSD([subQ0])],"isStart":false})});}
            var Q95;
            Q95=makeQuery(id+"Fou14xSP3GQJlB0_5.boolean.opBoolean","INTERSECT",EDGE,{"derivedFrom":[makeQuery(id+"F7.boolean.opBoolean","COPY",FACE,{"disambiguationData":[TD([makeQuery(id+"F3.opExtrude","SWEPT_FACE",FACE,{"disambiguationData":[OSD([sQuery(id+"F2.wireOp",EDGE,"0J23cXKG-jTpq-C0wa-xp2X-HWyvlrIdDXZe.left")])]})])],"derivedFrom":makeQuery(id+"F7.opExtrude","SWEPT_FACE",FACE,{"disambiguationData":[OSD([sQuery(id+"F6.wireOp",EDGE,"E37.MirrorCS")])]})}),makeQuery(id+"Fou14xSP3GQJlB0_5.opExtrude","SWEPT_FACE",FACE,{"disambiguationData":[OSD([sQuery(id+"Ffmn4ZGQaAwYWcj_5.wireOp",EDGE,"83f02070-e68f-438f-992c-3ac59f97bf76.0.2.3")])]})]});
            var Q96;
            {var subQ0=sQuery(id+"F2.wireOp",EDGE,"0J23cXKG-jTpq-C0wa-xp2X-HWyvlrIdDXZe.right");Q96=makeQuery(id+"F7.boolean.opBoolean","SPLIT",EDGE,{"disambiguationData":[TD([makeQuery(id+"F7.opExtrude","SWEPT_FACE",FACE,{"disambiguationData":[OSD([sQuery(id+"F6.wireOp",EDGE,"E21.MirrorCS")])]})])],"derivedFrom":makeQuery(id+"F3.opExtrude","CAP_EDGE",EDGE,{"disambiguationData":[OSD([subQ0])],"isStart":false})});}
            var Q97;
            Q97=makeQuery(id+"Fou14xSP3GQJlB0_5.boolean.opBoolean","INTERSECT",EDGE,{"derivedFrom":[makeQuery(id+"F7.boolean.opBoolean","COPY",FACE,{"disambiguationData":[TD([makeQuery(id+"F3.opExtrude","SWEPT_FACE",FACE,{"disambiguationData":[OSD([sQuery(id+"F2.wireOp",EDGE,"0J23cXKG-jTpq-C0wa-xp2X-HWyvlrIdDXZe.left")])]})])],"derivedFrom":makeQuery(id+"F7.opExtrude","SWEPT_FACE",FACE,{"disambiguationData":[OSD([sQuery(id+"F6.wireOp",EDGE,"E36.MirrorCS")])]})}),makeQuery(id+"Fou14xSP3GQJlB0_5.opExtrude","SWEPT_FACE",FACE,{"disambiguationData":[OSD([sQuery(id+"Ffmn4ZGQaAwYWcj_5.wireOp",EDGE,"83f02070-e68f-438f-992c-3ac59f97bf76.0.3.3")])]})]});
            var Q98;
            {var subQ0=sQuery(id+"F2.wireOp",EDGE,"0J23cXKG-jTpq-C0wa-xp2X-HWyvlrIdDXZe.right");Q98=makeQuery(id+"F7.boolean.opBoolean","SPLIT",EDGE,{"disambiguationData":[TD([makeQuery(id+"F7.opExtrude","SWEPT_FACE",FACE,{"disambiguationData":[OSD([sQuery(id+"F6.wireOp",EDGE,"E20.MirrorCS")])]})])],"derivedFrom":makeQuery(id+"F3.opExtrude","CAP_EDGE",EDGE,{"disambiguationData":[OSD([subQ0])],"isStart":false})});}
            var Q99;
            Q99=makeQuery(id+"Fou14xSP3GQJlB0_5.boolean.opBoolean","INTERSECT",EDGE,{"derivedFrom":[makeQuery(id+"F7.boolean.opBoolean","COPY",FACE,{"disambiguationData":[TD([makeQuery(id+"F3.opExtrude","SWEPT_FACE",FACE,{"disambiguationData":[OSD([sQuery(id+"F2.wireOp",EDGE,"0J23cXKG-jTpq-C0wa-xp2X-HWyvlrIdDXZe.left")])]})])],"derivedFrom":makeQuery(id+"F7.opExtrude","SWEPT_FACE",FACE,{"disambiguationData":[OSD([sQuery(id+"F6.wireOp",EDGE,"E28.MirrorCS")])]})}),makeQuery(id+"Fou14xSP3GQJlB0_5.opExtrude","SWEPT_FACE",FACE,{"disambiguationData":[OSD([sQuery(id+"Ffmn4ZGQaAwYWcj_5.wireOp",EDGE,"83f02070-e68f-438f-992c-3ac59f97bf76.0.4.3")])]})]});
            var Q100;
            {var subQ0=sQuery(id+"F2.wireOp",EDGE,"0J23cXKG-jTpq-C0wa-xp2X-HWyvlrIdDXZe.right");var subQ1=sQuery(id+"F2.wireOp",EDGE,"0J23cXKG-jTpq-C0wa-xp2X-HWyvlrIdDXZe.top");Q100=makeQuery(id+"F7.boolean.opBoolean","SPLIT",EDGE,{"disambiguationData":[TD([makeQuery(id+"F3.opExtrude","SWEPT_FACE",FACE,{"disambiguationData":[OSD([subQ1])]})])],"derivedFrom":makeQuery(id+"F3.opExtrude","CAP_EDGE",EDGE,{"disambiguationData":[OSD([subQ0])],"isStart":false})});}
            var Q101;
            {var subQ0=sQuery(id+"F2.wireOp",EDGE,"0J23cXKG-jTpq-C0wa-xp2X-HWyvlrIdDXZe.bottom");var subQ1=sQuery(id+"F2.wireOp",EDGE,"0J23cXKG-jTpq-C0wa-xp2X-HWyvlrIdDXZe.right");Q101=makeQuery(id+"F7.boolean.opBoolean","SPLIT",EDGE,{"disambiguationData":[TD([makeQuery(id+"F3.opExtrude","SWEPT_FACE",FACE,{"disambiguationData":[OSD([subQ0])]})])],"derivedFrom":makeQuery(id+"F3.opExtrude","CAP_EDGE",EDGE,{"disambiguationData":[OSD([subQ1])],"isStart":true})});}
            var Q102;
            Q102=makeQuery(id+"Fou14xSP3GQJlB0_5.boolean.opBoolean","INTERSECT",EDGE,{"derivedFrom":[makeQuery(id+"F7.boolean.opBoolean","COPY",FACE,{"disambiguationData":[TD([makeQuery(id+"F3.opExtrude","SWEPT_FACE",FACE,{"disambiguationData":[OSD([sQuery(id+"F2.wireOp",EDGE,"0J23cXKG-jTpq-C0wa-xp2X-HWyvlrIdDXZe.left")])]})])],"derivedFrom":makeQuery(id+"F7.opExtrude","SWEPT_FACE",FACE,{"disambiguationData":[OSD([sQuery(id+"F6.wireOp",EDGE,"E10.4.0.1")])]})}),makeQuery(id+"Fou14xSP3GQJlB0_5.opExtrude","SWEPT_FACE",FACE,{"disambiguationData":[OSD([sQuery(id+"Ffmn4ZGQaAwYWcj_5.wireOp",EDGE,"5qgGCEaO-EZzk-biRs-uW5n-FUkAzBEinMKw.left")])]})]});
            var Q103;
            {var subQ0=sQuery(id+"F2.wireOp",EDGE,"0J23cXKG-jTpq-C0wa-xp2X-HWyvlrIdDXZe.right");Q103=makeQuery(id+"F7.boolean.opBoolean","SPLIT",EDGE,{"disambiguationData":[TD([makeQuery(id+"F7.opExtrude","SWEPT_FACE",FACE,{"disambiguationData":[OSD([sQuery(id+"F6.wireOp",EDGE,"E10.3.0.0")])]})])],"derivedFrom":makeQuery(id+"F3.opExtrude","CAP_EDGE",EDGE,{"disambiguationData":[OSD([subQ0])],"isStart":true})});}
            var Q104;
            Q104=makeQuery(id+"Fou14xSP3GQJlB0_5.boolean.opBoolean","INTERSECT",EDGE,{"derivedFrom":[makeQuery(id+"F7.boolean.opBoolean","COPY",FACE,{"disambiguationData":[TD([makeQuery(id+"F3.opExtrude","SWEPT_FACE",FACE,{"disambiguationData":[OSD([sQuery(id+"F2.wireOp",EDGE,"0J23cXKG-jTpq-C0wa-xp2X-HWyvlrIdDXZe.left")])]})])],"derivedFrom":makeQuery(id+"F7.opExtrude","SWEPT_FACE",FACE,{"disambiguationData":[OSD([sQuery(id+"F6.wireOp",EDGE,"E10.3.0.1")])]})}),makeQuery(id+"Fou14xSP3GQJlB0_5.opExtrude","SWEPT_FACE",FACE,{"disambiguationData":[OSD([sQuery(id+"Ffmn4ZGQaAwYWcj_5.wireOp",EDGE,"83f02070-e68f-438f-992c-3ac59f97bf76.0.1.3")])]})]});
            var Q105;
            {var subQ0=sQuery(id+"F2.wireOp",EDGE,"0J23cXKG-jTpq-C0wa-xp2X-HWyvlrIdDXZe.right");Q105=makeQuery(id+"F7.boolean.opBoolean","SPLIT",EDGE,{"disambiguationData":[TD([makeQuery(id+"F7.opExtrude","SWEPT_FACE",FACE,{"disambiguationData":[OSD([sQuery(id+"F6.wireOp",EDGE,"E10.2.0.0")])]})])],"derivedFrom":makeQuery(id+"F3.opExtrude","CAP_EDGE",EDGE,{"disambiguationData":[OSD([subQ0])],"isStart":true})});}
            var Q106;
            Q106=makeQuery(id+"Fou14xSP3GQJlB0_5.boolean.opBoolean","INTERSECT",EDGE,{"derivedFrom":[makeQuery(id+"F7.boolean.opBoolean","COPY",FACE,{"disambiguationData":[TD([makeQuery(id+"F3.opExtrude","SWEPT_FACE",FACE,{"disambiguationData":[OSD([sQuery(id+"F2.wireOp",EDGE,"0J23cXKG-jTpq-C0wa-xp2X-HWyvlrIdDXZe.left")])]})])],"derivedFrom":makeQuery(id+"F7.opExtrude","SWEPT_FACE",FACE,{"disambiguationData":[OSD([sQuery(id+"F6.wireOp",EDGE,"E10.2.0.1")])]})}),makeQuery(id+"Fou14xSP3GQJlB0_5.opExtrude","SWEPT_FACE",FACE,{"disambiguationData":[OSD([sQuery(id+"Ffmn4ZGQaAwYWcj_5.wireOp",EDGE,"83f02070-e68f-438f-992c-3ac59f97bf76.0.2.3")])]})]});
            var Q107;
            {var subQ0=sQuery(id+"F2.wireOp",EDGE,"0J23cXKG-jTpq-C0wa-xp2X-HWyvlrIdDXZe.right");Q107=makeQuery(id+"F7.boolean.opBoolean","SPLIT",EDGE,{"disambiguationData":[TD([makeQuery(id+"F7.opExtrude","SWEPT_FACE",FACE,{"disambiguationData":[OSD([sQuery(id+"F6.wireOp",EDGE,"E10.1.0.0")])]})])],"derivedFrom":makeQuery(id+"F3.opExtrude","CAP_EDGE",EDGE,{"disambiguationData":[OSD([subQ0])],"isStart":true})});}
            var Q108;
            Q108=makeQuery(id+"Fou14xSP3GQJlB0_5.boolean.opBoolean","INTERSECT",EDGE,{"derivedFrom":[makeQuery(id+"F7.boolean.opBoolean","COPY",FACE,{"disambiguationData":[TD([makeQuery(id+"F3.opExtrude","SWEPT_FACE",FACE,{"disambiguationData":[OSD([sQuery(id+"F2.wireOp",EDGE,"0J23cXKG-jTpq-C0wa-xp2X-HWyvlrIdDXZe.left")])]})])],"derivedFrom":makeQuery(id+"F7.opExtrude","SWEPT_FACE",FACE,{"disambiguationData":[OSD([sQuery(id+"F6.wireOp",EDGE,"E10.1.0.1")])]})}),makeQuery(id+"Fou14xSP3GQJlB0_5.opExtrude","SWEPT_FACE",FACE,{"disambiguationData":[OSD([sQuery(id+"Ffmn4ZGQaAwYWcj_5.wireOp",EDGE,"83f02070-e68f-438f-992c-3ac59f97bf76.0.3.3")])]})]});
            var Q109;
            {var subQ0=sQuery(id+"F2.wireOp",EDGE,"0J23cXKG-jTpq-C0wa-xp2X-HWyvlrIdDXZe.right");Q109=makeQuery(id+"F7.boolean.opBoolean","SPLIT",EDGE,{"disambiguationData":[TD([makeQuery(id+"F7.opExtrude","SWEPT_FACE",FACE,{"disambiguationData":[OSD([sQuery(id+"F6.wireOp",EDGE,"E9")])]})])],"derivedFrom":makeQuery(id+"F3.opExtrude","CAP_EDGE",EDGE,{"disambiguationData":[OSD([subQ0])],"isStart":true})});}
            var Q110;
            Q110=makeQuery(id+"Fou14xSP3GQJlB0_5.boolean.opBoolean","INTERSECT",EDGE,{"derivedFrom":[makeQuery(id+"F7.boolean.opBoolean","COPY",FACE,{"disambiguationData":[TD([makeQuery(id+"F3.opExtrude","SWEPT_FACE",FACE,{"disambiguationData":[OSD([sQuery(id+"F2.wireOp",EDGE,"0J23cXKG-jTpq-C0wa-xp2X-HWyvlrIdDXZe.left")])]})])],"derivedFrom":makeQuery(id+"F7.opExtrude","SWEPT_FACE",FACE,{"disambiguationData":[OSD([sQuery(id+"F6.wireOp",EDGE,"E8")])]})}),makeQuery(id+"Fou14xSP3GQJlB0_5.opExtrude","SWEPT_FACE",FACE,{"disambiguationData":[OSD([sQuery(id+"Ffmn4ZGQaAwYWcj_5.wireOp",EDGE,"83f02070-e68f-438f-992c-3ac59f97bf76.0.4.3")])]})]});
            var Q111;
            {var subQ0=sQuery(id+"F2.wireOp",EDGE,"0J23cXKG-jTpq-C0wa-xp2X-HWyvlrIdDXZe.right");var subQ1=sQuery(id+"F2.wireOp",EDGE,"0J23cXKG-jTpq-C0wa-xp2X-HWyvlrIdDXZe.top");Q111=makeQuery(id+"F7.boolean.opBoolean","SPLIT",EDGE,{"disambiguationData":[TD([makeQuery(id+"F3.opExtrude","SWEPT_FACE",FACE,{"disambiguationData":[OSD([subQ1])]})])],"derivedFrom":makeQuery(id+"F3.opExtrude","CAP_EDGE",EDGE,{"disambiguationData":[OSD([subQ0])],"isStart":true})});}
            var Q112;
            {var subQ0=sQuery(id+"F2.wireOp",EDGE,"kwgpZEqd-2C8t-yznH-LOjq-w4z4yBxY72GK.bottom");var subQ1=sQuery(id+"F2.wireOp",EDGE,"kwgpZEqd-2C8t-yznH-LOjq-w4z4yBxY72GK.left");Q112=makeQuery(id+"F7.boolean.opBoolean","SPLIT",EDGE,{"disambiguationData":[TD([makeQuery(id+"F3.opExtrude","SWEPT_FACE",FACE,{"disambiguationData":[OSD([subQ0])]})])],"derivedFrom":makeQuery(id+"F3.opExtrude","CAP_EDGE",EDGE,{"disambiguationData":[OSD([subQ1])],"isStart":true})});}
            var Q113;
            {var subQ0=sQuery(id+"F2.wireOp",EDGE,"kwgpZEqd-2C8t-yznH-LOjq-w4z4yBxY72GK.left");Q113=makeQuery(id+"F7.boolean.opBoolean","SPLIT",EDGE,{"disambiguationData":[TD([makeQuery(id+"F7.opExtrude","SWEPT_FACE",FACE,{"disambiguationData":[OSD([sQuery(id+"F6.wireOp",EDGE,"E10.3.0.0")])]})])],"derivedFrom":makeQuery(id+"F3.opExtrude","CAP_EDGE",EDGE,{"disambiguationData":[OSD([subQ0])],"isStart":true})});}
            var Q114;
            {var subQ0=sQuery(id+"F2.wireOp",EDGE,"kwgpZEqd-2C8t-yznH-LOjq-w4z4yBxY72GK.left");Q114=makeQuery(id+"F7.boolean.opBoolean","SPLIT",EDGE,{"disambiguationData":[TD([makeQuery(id+"F7.opExtrude","SWEPT_FACE",FACE,{"disambiguationData":[OSD([sQuery(id+"F6.wireOp",EDGE,"E10.2.0.0")])]})])],"derivedFrom":makeQuery(id+"F3.opExtrude","CAP_EDGE",EDGE,{"disambiguationData":[OSD([subQ0])],"isStart":true})});}
            var Q115;
            Q115=makeQuery(id+"F7.boolean.opBoolean","INTERSECT",EDGE,{"derivedFrom":[makeQuery(id+"F3.opExtrude","SWEPT_FACE",FACE,{"disambiguationData":[OSD([sQuery(id+"F2.wireOp",EDGE,"kwgpZEqd-2C8t-yznH-LOjq-w4z4yBxY72GK.left")])]}),makeQuery(id+"F7.opExtrude","SWEPT_FACE",FACE,{"disambiguationData":[OSD([sQuery(id+"F6.wireOp",EDGE,"E10.3.0.1")])]})]});
            var Q116;
            Q116=makeQuery(id+"F7.boolean.opBoolean","INTERSECT",EDGE,{"derivedFrom":[makeQuery(id+"F3.opExtrude","SWEPT_FACE",FACE,{"disambiguationData":[OSD([sQuery(id+"F2.wireOp",EDGE,"kwgpZEqd-2C8t-yznH-LOjq-w4z4yBxY72GK.left")])]}),makeQuery(id+"F7.opExtrude","SWEPT_FACE",FACE,{"disambiguationData":[OSD([sQuery(id+"F6.wireOp",EDGE,"E10.4.0.1")])]})]});
            var Q117;
            Q117=makeQuery(id+"F7.boolean.opBoolean","INTERSECT",EDGE,{"derivedFrom":[makeQuery(id+"F3.opExtrude","SWEPT_FACE",FACE,{"disambiguationData":[OSD([sQuery(id+"F2.wireOp",EDGE,"kwgpZEqd-2C8t-yznH-LOjq-w4z4yBxY72GK.left")])]}),makeQuery(id+"F7.opExtrude","SWEPT_FACE",FACE,{"disambiguationData":[OSD([sQuery(id+"F6.wireOp",EDGE,"E10.2.0.1")])]})]});
            var Q118;
            {var subQ0=sQuery(id+"F2.wireOp",EDGE,"kwgpZEqd-2C8t-yznH-LOjq-w4z4yBxY72GK.left");Q118=makeQuery(id+"F7.boolean.opBoolean","SPLIT",EDGE,{"disambiguationData":[TD([makeQuery(id+"F7.opExtrude","SWEPT_FACE",FACE,{"disambiguationData":[OSD([sQuery(id+"F6.wireOp",EDGE,"E10.1.0.0")])]})])],"derivedFrom":makeQuery(id+"F3.opExtrude","CAP_EDGE",EDGE,{"disambiguationData":[OSD([subQ0])],"isStart":true})});}
            var Q119;
            Q119=makeQuery(id+"F7.boolean.opBoolean","INTERSECT",EDGE,{"derivedFrom":[makeQuery(id+"F3.opExtrude","SWEPT_FACE",FACE,{"disambiguationData":[OSD([sQuery(id+"F2.wireOp",EDGE,"kwgpZEqd-2C8t-yznH-LOjq-w4z4yBxY72GK.left")])]}),makeQuery(id+"F7.opExtrude","SWEPT_FACE",FACE,{"disambiguationData":[OSD([sQuery(id+"F6.wireOp",EDGE,"E10.1.0.1")])]})]});
            var Q120;
            {var subQ0=sQuery(id+"F2.wireOp",EDGE,"kwgpZEqd-2C8t-yznH-LOjq-w4z4yBxY72GK.left");Q120=makeQuery(id+"F7.boolean.opBoolean","SPLIT",EDGE,{"disambiguationData":[TD([makeQuery(id+"F7.opExtrude","SWEPT_FACE",FACE,{"disambiguationData":[OSD([sQuery(id+"F6.wireOp",EDGE,"E9")])]})])],"derivedFrom":makeQuery(id+"F3.opExtrude","CAP_EDGE",EDGE,{"disambiguationData":[OSD([subQ0])],"isStart":true})});}
            var Q121;
            Q121=makeQuery(id+"F7.boolean.opBoolean","INTERSECT",EDGE,{"derivedFrom":[makeQuery(id+"F3.opExtrude","SWEPT_FACE",FACE,{"disambiguationData":[OSD([sQuery(id+"F2.wireOp",EDGE,"kwgpZEqd-2C8t-yznH-LOjq-w4z4yBxY72GK.left")])]}),makeQuery(id+"F7.opExtrude","SWEPT_FACE",FACE,{"disambiguationData":[OSD([sQuery(id+"F6.wireOp",EDGE,"E8")])]})]});
            var Q122;
            {var subQ0=sQuery(id+"F2.wireOp",EDGE,"kwgpZEqd-2C8t-yznH-LOjq-w4z4yBxY72GK.left");var subQ1=sQuery(id+"F2.wireOp",EDGE,"kwgpZEqd-2C8t-yznH-LOjq-w4z4yBxY72GK.top");Q122=makeQuery(id+"F7.boolean.opBoolean","SPLIT",EDGE,{"disambiguationData":[TD([makeQuery(id+"F3.opExtrude","SWEPT_FACE",FACE,{"disambiguationData":[OSD([subQ1])]})])],"derivedFrom":makeQuery(id+"F3.opExtrude","CAP_EDGE",EDGE,{"disambiguationData":[OSD([subQ0])],"isStart":true})});}
            var Q123;
            Q123=makeQuery(id+"F1.opExtrude","SWEPT_EDGE",EDGE,{"disambiguationData":[OSD([sQuery(id+"F0.wireOp",EDGE,"E0.bottom"),sQuery(id+"F0.wireOp",EDGE,"E0.right")])]});
            var Q124;
            {var subQ0=sQuery(id+"F2.wireOp",EDGE,"0J23cXKG-jTpq-C0wa-xp2X-HWyvlrIdDXZe.bottom");var subQ1=sQuery(id+"F2.wireOp",EDGE,"0J23cXKG-jTpq-C0wa-xp2X-HWyvlrIdDXZe.left");Q124=makeQuery(id+"F7.boolean.opBoolean","SPLIT",EDGE,{"disambiguationData":[TD([makeQuery(id+"F3.opExtrude","SWEPT_FACE",FACE,{"disambiguationData":[OSD([subQ0])]})])],"derivedFrom":makeQuery(id+"F3.opExtrude","CAP_EDGE",EDGE,{"disambiguationData":[OSD([subQ1])],"isStart":true})});}
            var Q125;
            {var subQ0=sQuery(id+"F2.wireOp",EDGE,"0J23cXKG-jTpq-C0wa-xp2X-HWyvlrIdDXZe.left");Q125=makeQuery(id+"F7.boolean.opBoolean","SPLIT",EDGE,{"disambiguationData":[TD([makeQuery(id+"F7.opExtrude","SWEPT_FACE",FACE,{"disambiguationData":[OSD([sQuery(id+"F6.wireOp",EDGE,"E10.3.0.0")])]})])],"derivedFrom":makeQuery(id+"F3.opExtrude","CAP_EDGE",EDGE,{"disambiguationData":[OSD([subQ0])],"isStart":true})});}
            var Q126;
            {var subQ0=sQuery(id+"F2.wireOp",EDGE,"0J23cXKG-jTpq-C0wa-xp2X-HWyvlrIdDXZe.left");Q126=makeQuery(id+"F7.boolean.opBoolean","SPLIT",EDGE,{"disambiguationData":[TD([makeQuery(id+"F7.opExtrude","SWEPT_FACE",FACE,{"disambiguationData":[OSD([sQuery(id+"F6.wireOp",EDGE,"E10.2.0.0")])]})])],"derivedFrom":makeQuery(id+"F3.opExtrude","CAP_EDGE",EDGE,{"disambiguationData":[OSD([subQ0])],"isStart":true})});}
            var Q127;
            {var subQ0=sQuery(id+"F2.wireOp",EDGE,"0J23cXKG-jTpq-C0wa-xp2X-HWyvlrIdDXZe.left");Q127=makeQuery(id+"F7.boolean.opBoolean","SPLIT",EDGE,{"disambiguationData":[TD([makeQuery(id+"F7.opExtrude","SWEPT_FACE",FACE,{"disambiguationData":[OSD([sQuery(id+"F6.wireOp",EDGE,"E10.1.0.0")])]})])],"derivedFrom":makeQuery(id+"F3.opExtrude","CAP_EDGE",EDGE,{"disambiguationData":[OSD([subQ0])],"isStart":true})});}
            var Q128;
            {var subQ0=sQuery(id+"F2.wireOp",EDGE,"0J23cXKG-jTpq-C0wa-xp2X-HWyvlrIdDXZe.left");Q128=makeQuery(id+"F7.boolean.opBoolean","SPLIT",EDGE,{"disambiguationData":[TD([makeQuery(id+"F7.opExtrude","SWEPT_FACE",FACE,{"disambiguationData":[OSD([sQuery(id+"F6.wireOp",EDGE,"E9")])]})])],"derivedFrom":makeQuery(id+"F3.opExtrude","CAP_EDGE",EDGE,{"disambiguationData":[OSD([subQ0])],"isStart":true})});}
            var Q129;
            {var subQ0=sQuery(id+"F2.wireOp",EDGE,"0J23cXKG-jTpq-C0wa-xp2X-HWyvlrIdDXZe.left");var subQ1=sQuery(id+"F2.wireOp",EDGE,"0J23cXKG-jTpq-C0wa-xp2X-HWyvlrIdDXZe.top");Q129=makeQuery(id+"F7.boolean.opBoolean","SPLIT",EDGE,{"disambiguationData":[TD([makeQuery(id+"F3.opExtrude","SWEPT_FACE",FACE,{"disambiguationData":[OSD([subQ1])]})])],"derivedFrom":makeQuery(id+"F3.opExtrude","CAP_EDGE",EDGE,{"disambiguationData":[OSD([subQ0])],"isStart":true})});}
            var Q130;
            Q130=makeQuery(id+"F1.opExtrude","SWEPT_EDGE",EDGE,{"disambiguationData":[OSD([sQuery(id+"F0.wireOp",EDGE,"E0.bottom"),sQuery(id+"F0.wireOp",EDGE,"E0.left")])]});
            var Q131;
            Q131=makeQuery(id+"F7.boolean.opBoolean","INTERSECT",EDGE,{"derivedFrom":[makeQuery(id+"F3.opExtrude","SWEPT_FACE",FACE,{"disambiguationData":[OSD([sQuery(id+"F2.wireOp",EDGE,"0J23cXKG-jTpq-C0wa-xp2X-HWyvlrIdDXZe.left")])]}),makeQuery(id+"F7.opExtrude","SWEPT_FACE",FACE,{"disambiguationData":[OSD([sQuery(id+"F6.wireOp",EDGE,"E8")])]})]});
            var Q132;
            Q132=makeQuery(id+"F7.boolean.opBoolean","INTERSECT",EDGE,{"derivedFrom":[makeQuery(id+"F3.opExtrude","SWEPT_FACE",FACE,{"disambiguationData":[OSD([sQuery(id+"F2.wireOp",EDGE,"0J23cXKG-jTpq-C0wa-xp2X-HWyvlrIdDXZe.left")])]}),makeQuery(id+"F7.opExtrude","SWEPT_FACE",FACE,{"disambiguationData":[OSD([sQuery(id+"F6.wireOp",EDGE,"E10.1.0.1")])]})]});
            var Q133;
            Q133=makeQuery(id+"F7.boolean.opBoolean","INTERSECT",EDGE,{"derivedFrom":[makeQuery(id+"F3.opExtrude","SWEPT_FACE",FACE,{"disambiguationData":[OSD([sQuery(id+"F2.wireOp",EDGE,"0J23cXKG-jTpq-C0wa-xp2X-HWyvlrIdDXZe.left")])]}),makeQuery(id+"F7.opExtrude","SWEPT_FACE",FACE,{"disambiguationData":[OSD([sQuery(id+"F6.wireOp",EDGE,"E10.2.0.1")])]})]});
            var Q134;
            Q134=makeQuery(id+"F7.boolean.opBoolean","INTERSECT",EDGE,{"derivedFrom":[makeQuery(id+"F3.opExtrude","SWEPT_FACE",FACE,{"disambiguationData":[OSD([sQuery(id+"F2.wireOp",EDGE,"0J23cXKG-jTpq-C0wa-xp2X-HWyvlrIdDXZe.left")])]}),makeQuery(id+"F7.opExtrude","SWEPT_FACE",FACE,{"disambiguationData":[OSD([sQuery(id+"F6.wireOp",EDGE,"E10.3.0.1")])]})]});
            var Q135;
            Q135=makeQuery(id+"F7.boolean.opBoolean","INTERSECT",EDGE,{"derivedFrom":[makeQuery(id+"F3.opExtrude","SWEPT_FACE",FACE,{"disambiguationData":[OSD([sQuery(id+"F2.wireOp",EDGE,"0J23cXKG-jTpq-C0wa-xp2X-HWyvlrIdDXZe.left")])]}),makeQuery(id+"F7.opExtrude","SWEPT_FACE",FACE,{"disambiguationData":[OSD([sQuery(id+"F6.wireOp",EDGE,"E10.4.0.1")])]})]});
            fillet(context, id + "F26", {"entities" : qUnion([Q0, Q1, Q2, Q3, Q4, Q5, Q6, Q7, Q8, Q9, Q10, Q11, Q12, Q13, Q14, Q15, Q16, Q17, Q18, Q19, Q20, Q21, Q22, Q23, Q24, Q25, Q26, Q27, Q28, Q29, Q30, Q31, Q32, Q33, Q34, Q35, Q36, Q37, Q38, Q39, Q40, Q41, Q42, Q43, Q44, Q45, Q46, Q47, Q48, Q49, Q50, Q51, Q52, Q53, Q54, Q55, Q56, Q57, Q58, Q59, Q60, Q61, Q62, Q63, Q64, Q65, Q66, Q67, Q68, Q69, Q70, Q71, Q72, Q73, Q74, Q75, Q76, Q77, Q78, Q79, Q80, Q81, Q82, Q83, Q84, Q85, Q86, Q87, Q88, Q89, Q90, Q91, Q92, Q93, Q94, Q95, Q96, Q97, Q98, Q99, Q100, Q101, Q102, Q103, Q104, Q105, Q106, Q107, Q108, Q109, Q110, Q111, Q112, Q113, Q114, Q115, Q116, Q117, Q118, Q119, Q120, Q121, Q122, Q123, Q124, Q125, Q126, Q127, Q128, Q129, Q130, Q131, Q132, Q133, Q134, Q135]), "radius" : 2 * mm, "tangentPropagation" : true, "allowEdgeOverflow" : false});
        }
    });
